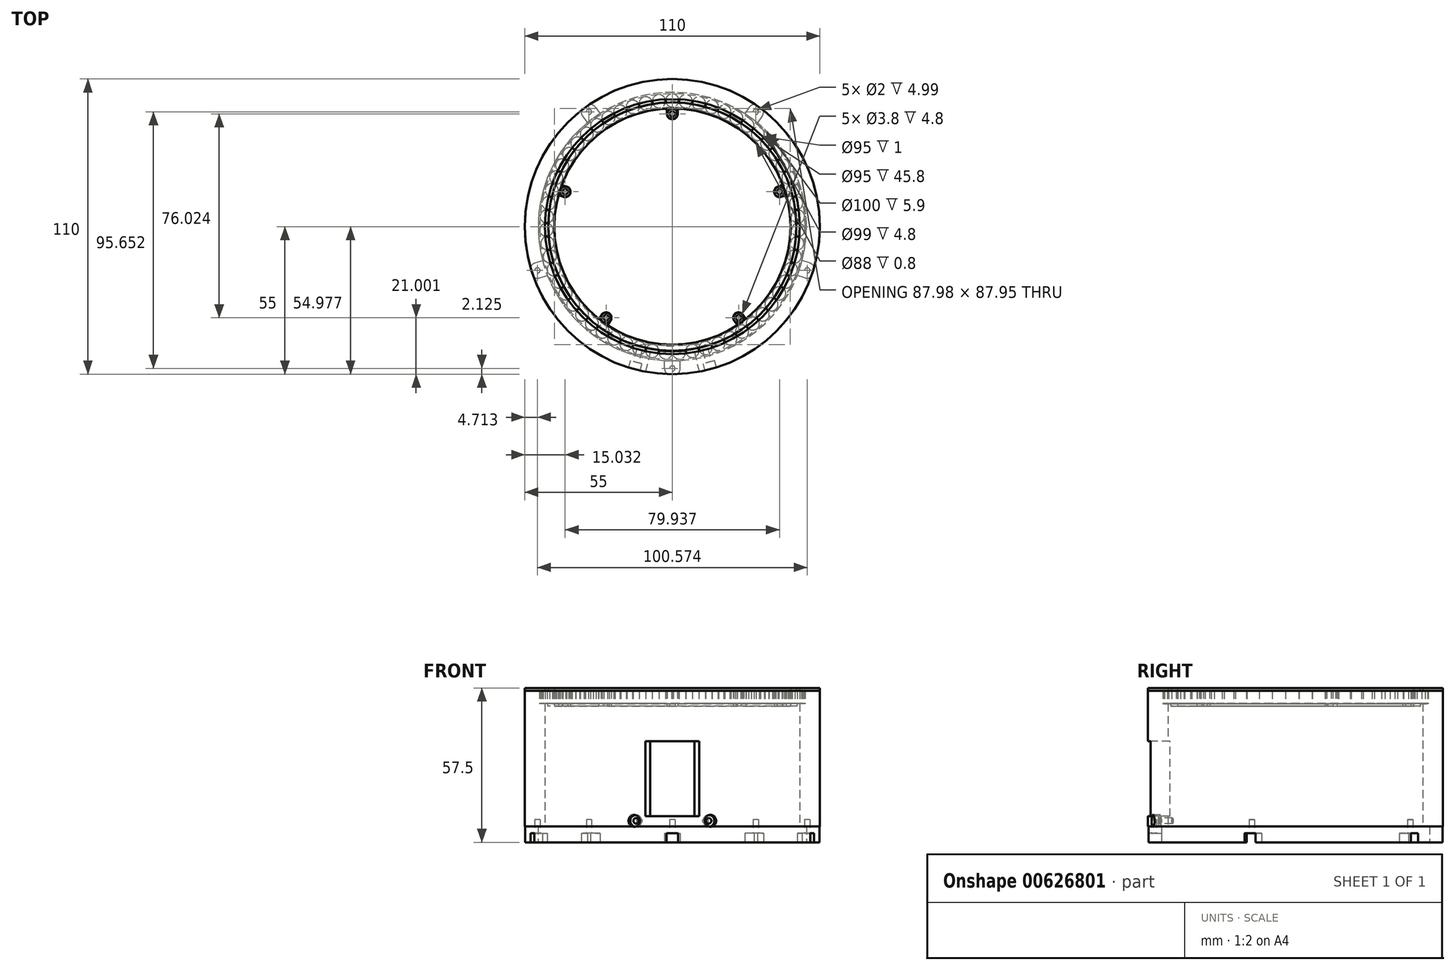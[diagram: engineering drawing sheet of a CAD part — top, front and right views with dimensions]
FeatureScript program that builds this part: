
annotation { "Feature Type Name" : "Feature", "Feature Type Description" : "" }
export const myFeature = defineFeature(function(context is Context, id is Id, definition is map)
    precondition{}
    {
        {
            var Q0;
            Q0=qCreatedBy(makeId("Top.planeOp"),FACE);
            var sketch = newSketch(context, id + "F0", { "sketchPlane" : qUnion([Q0])});
            skCircle(sketch, "E0", {"center": v(0, 0) * mm, "radius": 54.84 * mm});
            skCircle(sketch, "E1", {"center": v(0, 0) * mm, "radius": 50 * mm});
            skLineSegment(sketch, "E2", {"start": v(0, 0) * mm, "end": v(0, -52.87) * mm, "construction": true});
            skCircle(sketch, "E3", {"center": v(0, -52.88) * mm, "radius": 1 * mm});
            skCircle(sketch, "E4.1.0", {"center": v(50.29, -16.34) * mm, "radius": 1 * mm});
            skCircle(sketch, "E4.2.0", {"center": v(31.08, 42.78) * mm, "radius": 1 * mm});
            skCircle(sketch, "E4.3.0", {"center": v(-31.08, 42.78) * mm, "radius": 1 * mm});
            skCircle(sketch, "E4.4.0", {"center": v(-50.29, -16.34) * mm, "radius": 1 * mm});
            skCircle(sketch, "E5", {"center": v(0, -52.88) * mm, "radius": 2.9 * mm});
            skLineSegment(sketch, "E6", {"start": v(2.9, -52.88) * mm, "end": v(2.9, -49.89) * mm});
            skLineSegment(sketch, "E7.1.0", {"start": v(49.4, -19.1) * mm, "end": v(46.6, -18.19) * mm});
            skLineSegment(sketch, "E7.1.1", {"start": v(51.18, -13.58) * mm, "end": v(48.34, -12.66) * mm});
            skCircle(sketch, "E7.1.2", {"center": v(50.29, -16.34) * mm, "radius": 2.9 * mm});
            skLineSegment(sketch, "E7.2.0", {"start": v(33.43, 41.07) * mm, "end": v(31.7, 38.7) * mm});
            skLineSegment(sketch, "E7.2.1", {"start": v(28.73, 44.48) * mm, "end": v(26.98, 42.06) * mm});
            skCircle(sketch, "E7.2.2", {"center": v(31.08, 42.78) * mm, "radius": 2.9 * mm});
            skLineSegment(sketch, "E7.3.0", {"start": v(-28.73, 44.48) * mm, "end": v(-27, 42.1) * mm});
            skLineSegment(sketch, "E7.3.1", {"start": v(-33.43, 41.07) * mm, "end": v(-31.67, 38.65) * mm});
            skCircle(sketch, "E7.3.2", {"center": v(-31.08, 42.78) * mm, "radius": 2.9 * mm});
            skLineSegment(sketch, "E7.4.0", {"start": v(-51.18, -13.58) * mm, "end": v(-48.39, -12.67) * mm});
            skLineSegment(sketch, "E7.4.1", {"start": v(-49.4, -19.1) * mm, "end": v(-46.55, -18.17) * mm});
            skCircle(sketch, "E7.4.2", {"center": v(-50.29, -16.34) * mm, "radius": 2.9 * mm});
            skLineSegment(sketch, "E8", {"start": v(-2.9, -52.88) * mm, "end": v(-2.9, -49.92) * mm});
            skLineSegment(sketch, "E9.1.0", {"start": v(49.4, -19.1) * mm, "end": v(46.58, -18.18) * mm});
            skLineSegment(sketch, "E9.2.0", {"start": v(33.43, 41.07) * mm, "end": v(31.69, 38.68) * mm});
            skLineSegment(sketch, "E9.3.0", {"start": v(-28.73, 44.48) * mm, "end": v(-27, 42.09) * mm});
            skLineSegment(sketch, "E9.4.0", {"start": v(-51.18, -13.58) * mm, "end": v(-48.37, -12.67) * mm});
            skSolve(sketch);
        }
        {
            var Q0;
            {var subQ0=sQuery(id+"F0.wireOp",EDGE,"E8");Q0=makeQuery(id+"F0.imprint","IMPRINT",FACE,{"disambiguationData":[TD([[makeQuery(id+"F0.imprint","IMPRINT",EDGE,{"derivedFrom":subQ0}),1.0]])]});}
            var Q1;
            {var subQ9=sQuery(id+"F0.wireOp",EDGE,"E9.1.0");var subQ12=makeQuery(id+"F0.imprint","IMPRINT",VERTEX,{"derivedFrom":subQ9});Q1=makeQuery(id+"F0.imprint","IMPRINT",FACE,{"disambiguationData":[TD([[makeQuery(id+"F0.imprint","IMPRINT",EDGE,{"disambiguationData":[TD([[subQ12,1.0]])],"derivedFrom":subQ9}),1.0]])]});}
            var Q2;
            {var subQ7=sQuery(id+"F0.wireOp",EDGE,"E9.4.0");var subQ12=makeQuery(id+"F0.imprint","IMPRINT",VERTEX,{"derivedFrom":subQ7});Q2=makeQuery(id+"F0.imprint","IMPRINT",FACE,{"disambiguationData":[TD([[makeQuery(id+"F0.imprint","IMPRINT",EDGE,{"disambiguationData":[TD([[subQ12,1.0]])],"derivedFrom":subQ7}),1.0]])]});}
            var Q3;
            {var subQ5=sQuery(id+"F0.wireOp",EDGE,"E9.2.0");var subQ11=makeQuery(id+"F0.imprint","IMPRINT",VERTEX,{"derivedFrom":subQ5});Q3=makeQuery(id+"F0.imprint","IMPRINT",FACE,{"disambiguationData":[TD([[makeQuery(id+"F0.imprint","IMPRINT",EDGE,{"disambiguationData":[TD([[subQ11,1.0]])],"derivedFrom":subQ5}),1.0]])]});}
            var Q4;
            {var subQ7=sQuery(id+"F0.wireOp",EDGE,"E9.3.0");var subQ12=makeQuery(id+"F0.imprint","IMPRINT",VERTEX,{"derivedFrom":subQ7});Q4=makeQuery(id+"F0.imprint","IMPRINT",FACE,{"disambiguationData":[TD([[makeQuery(id+"F0.imprint","IMPRINT",EDGE,{"disambiguationData":[TD([[subQ12,1.0]])],"derivedFrom":subQ7}),1.0]])]});}
            extrude(context, id + "F1", {"entities" : qUnion([Q0, Q1, Q2, Q3, Q4]), "depth" : 3.5 * mm, "offsetDistance" : 25 * mm, "hasSecondDirection" : true, "secondDirectionOppositeDirection" : false, "secondDirectionDepth" : 0.1 * mm});
        }
        {
            var Q0;
            Q0=makeQuery(id+"F1.opExtrude","CAP_FACE",FACE,{"disambiguationData":[OSD([sQuery(id+"F0.wireOp",EDGE,"E0"),sQuery(id+"F0.wireOp",EDGE,"E1"),sQuery(id+"F0.wireOp",EDGE,"E7.3.1"),sQuery(id+"F0.wireOp",EDGE,"E7.3.2"),sQuery(id+"F0.wireOp",EDGE,"E9.4.0"),sQuery(id+"F0.wireOp",EDGE,"E7.4.2")])],"isStart":false});
            var sketch = newSketch(context, id + "F2", { "sketchPlane" : qUnion([Q0])});
            skCircle(sketch, "E10", {"center": v(0, 0) * mm, "radius": 54.84 * mm});
            skCircle(sketch, "E11", {"center": v(0, 0) * mm, "radius": 50 * mm});
            skLineSegment(sketch, "E12", {"start": v(0, 0) * mm, "end": v(0, -52.88) * mm, "construction": true});
            skCircle(sketch, "E13", {"center": v(0, -52.88) * mm, "radius": 1 * mm});
            skCircle(sketch, "E14.1.0", {"center": v(50.29, -16.34) * mm, "radius": 1 * mm});
            skCircle(sketch, "E14.2.0", {"center": v(31.08, 42.78) * mm, "radius": 1 * mm});
            skCircle(sketch, "E14.3.0", {"center": v(-31.08, 42.78) * mm, "radius": 1 * mm});
            skCircle(sketch, "E14.4.0", {"center": v(-50.29, -16.34) * mm, "radius": 1 * mm});
            skSolve(sketch);
        }
        {
            var Q0;
            Q0=makeQuery(id+"F2.imprint","IMPRINT",FACE,{"disambiguationData":[TD([[makeQuery(id+"F2.imprint","IMPRINT",EDGE,{"derivedFrom":sQuery(id+"F2.wireOp",EDGE,"E13")}),-1.0]])]});
            var Q1;
            {var subQ1=sQuery(id+"F0.wireOp",EDGE,"E7.3.1");var subQ7=makeQuery(id+"F1.opExtrude","CAP_EDGE",EDGE,{"disambiguationData":[OSD([subQ1])],"isStart":false});Q1=makeQuery(id+"F2.imprint","IMPRINT",FACE,{"disambiguationData":[TD([[makeQuery(id+"F2.imprint","IMPRINT",EDGE,{"derivedFrom":subQ7}),-1.0]])]});}
            extrude(context, id + "F3", {"entities" : qUnion([Q0, Q1]), "operationType" : NewBodyOperationType.ADD, "depth" : 2.5 * mm, "offsetDistance" : 25 * mm});
        }
        {
            var Q0;
            Q0=makeQuery(id+"F3.opExtrude","CAP_FACE",FACE,{"disambiguationData":[OSD([sQuery(id+"F2.wireOp",EDGE,"E10"),sQuery(id+"F2.wireOp",EDGE,"E11"),sQuery(id+"F2.wireOp",EDGE,"E13"),sQuery(id+"F2.wireOp",EDGE,"E14.1.0"),sQuery(id+"F2.wireOp",EDGE,"E14.2.0"),sQuery(id+"F2.wireOp",EDGE,"E14.3.0"),sQuery(id+"F2.wireOp",EDGE,"E14.4.0")])],"isStart":false});
            var sketch = newSketch(context, id + "F4", { "sketchPlane" : qUnion([Q0])});
            skCircle(sketch, "E15", {"center": v(0, 0) * mm, "radius": 55 * mm});
            skCircle(sketch, "E16", {"center": v(0, 0) * mm, "radius": 47.5 * mm});
            skLineSegment(sketch, "E17", {"start": v(0, 0) * mm, "end": v(0, -52.88) * mm, "construction": true});
            skCircle(sketch, "E18", {"center": v(0, -52.88) * mm, "radius": 1 * mm});
            skCircle(sketch, "E19.1.0", {"center": v(50.29, -16.34) * mm, "radius": 1 * mm});
            skCircle(sketch, "E19.2.0", {"center": v(31.08, 42.78) * mm, "radius": 1 * mm});
            skCircle(sketch, "E19.3.0", {"center": v(-31.08, 42.78) * mm, "radius": 1 * mm});
            skCircle(sketch, "E19.4.0", {"center": v(-50.29, -16.34) * mm, "radius": 1 * mm});
            skSolve(sketch);
        }
        {
            var Q0;
            Q0 = qSketchRegion(id + "F4", true);
            extrude(context, id + "F5", {"entities" : qUnion([Q0]), "operationType" : NewBodyOperationType.ADD, "depth" : 2.5 * mm, "offsetDistance" : 25 * mm});
        }
        {
            var Q0;
            Q0=makeQuery(id+"F5.opExtrude","CAP_FACE",FACE,{"disambiguationData":[OSD([sQuery(id+"F4.wireOp",EDGE,"E15"),sQuery(id+"F4.wireOp",EDGE,"E16"),sQuery(id+"F4.wireOp",EDGE,"E18"),sQuery(id+"F4.wireOp",EDGE,"E19.1.0"),sQuery(id+"F4.wireOp",EDGE,"E19.2.0"),sQuery(id+"F4.wireOp",EDGE,"E19.3.0"),sQuery(id+"F4.wireOp",EDGE,"E19.4.0")])],"isStart":false});
            var sketch = newSketch(context, id + "F6", { "sketchPlane" : qUnion([Q0])});
            skCircle(sketch, "E20", {"center": v(0, 0) * mm, "radius": 55 * mm});
            skCircle(sketch, "E21", {"center": v(0, 0) * mm, "radius": 47.5 * mm});
            skSolve(sketch);
        }
        {
            var Q0;
            Q0 = qSketchRegion(id + "F6", true);
            extrude(context, id + "F7", {"entities" : qUnion([Q0]), "operationType" : NewBodyOperationType.ADD, "depth" : 42.3 * mm, "offsetDistance" : 25 * mm});
        }
        {
            var Q0;
            Q0=makeQuery(id+"F7.opExtrude","CAP_FACE",FACE,{"disambiguationData":[OSD([sQuery(id+"F6.wireOp",EDGE,"E20"),sQuery(id+"F6.wireOp",EDGE,"E21")])],"isStart":false});
            var sketch = newSketch(context, id + "F8", { "sketchPlane" : qUnion([Q0])});
            skLineSegment(sketch, "E22", {"start": v(0, 0) * mm, "end": v(0, -55) * mm, "construction": true});
            skCircle(sketch, "E23", {"center": v(0, 0) * mm, "radius": 55 * mm});
            skCircle(sketch, "E24", {"center": v(0, 0) * mm, "radius": 47.5 * mm});
            skLineSegment(sketch, "E25", {"start": v(0, 0) * mm, "end": v(8.25, -46.78) * mm, "construction": true});
            skLineSegment(sketch, "E26", {"start": v(0, 0) * mm, "end": v(-8.25, -46.78) * mm, "construction": true});
            skLineSegment(sketch, "E27", {"start": v(-8.25, -46.78) * mm, "end": v(-10, -54.08) * mm});
            skLineSegment(sketch, "E28", {"start": v(8.25, -46.78) * mm, "end": v(10, -54.08) * mm});
            skSolve(sketch);
        }
        {
            var Q0;
            {var subQ0=sQuery(id+"F8.wireOp",EDGE,"E27");Q0=makeQuery(id+"F8.imprint","IMPRINT",FACE,{"disambiguationData":[TD([[makeQuery(id+"F8.imprint","IMPRINT",EDGE,{"derivedFrom":subQ0}),1.0]])]});}
            extrude(context, id + "F9", {"entities" : qUnion([Q0]), "operationType" : NewBodyOperationType.REMOVE, "oppositeDirection" : true, "depth" : 41 * mm, "offsetDistance" : 25 * mm, "hasSecondDirection" : true, "secondDirectionOppositeDirection" : true, "secondDirectionDepth" : 13 * mm});
        }
        {
            var Q0;
            Q0=qCreatedBy(makeId("Front.planeOp"),FACE);
            var sketch = newSketch(context, id + "F10", { "sketchPlane" : qUnion([Q0])});
            skLineSegment(sketch, "E29", {"start": v(0, 0) * mm, "end": v(0, 3.5) * mm, "construction": true});
            skLineSegment(sketch, "E30", {"start": v(0, 3.5) * mm, "end": v(0, 8.1) * mm, "construction": true});
            skSolve(sketch);
        }
        {
            var Q0;
            Q0=qCreatedBy(makeId("Top.planeOp"),FACE);
            cPlane(context, id + "F11", {"entities" : qUnion([Q0]), "cplaneType" : CPlaneType.OFFSET, "offset" : 8.1 * mm, "width" : 150 * mm, "height" : 150 * mm});
        }
        {
            var Q0;
            Q0=qCreatedBy(id+"F11.planeOp",FACE);
            var sketch = newSketch(context, id + "F12", { "sketchPlane" : qUnion([Q0])});
            skLineSegment(sketch, "E31", {"start": v(0, 0) * mm, "end": v(0, -55.35) * mm, "construction": true});
            skCircle(sketch, "E32", {"center": v(0, 0) * mm, "radius": 55.35 * mm, "construction": true});
            skLineSegment(sketch, "E33", {"start": v(0, 0) * mm, "end": v(-14.33, -53.46) * mm, "construction": true});
            skLineSegment(sketch, "E34", {"start": v(0, 0) * mm, "end": v(14.33, -53.46) * mm, "construction": true});
            skLineSegment(sketch, "E35", {"start": v(-0.35, -57.2) * mm, "end": v(-14.33, -53.46) * mm, "construction": true});
            skLineSegment(sketch, "E36", {"start": v(14.33, -53.46) * mm, "end": v(0.35, -57.2) * mm, "construction": true});
            skSolve(sketch);
        }
        {
            var Q0;
            Q0=sQuery(id+"F12.wireOp",EDGE,"E35");
            cPlane(context, id + "F13", {"entities" : qUnion([Q0]), "cplaneType" : CPlaneType.LINE_ANGLE, "offset" : 25 * mm, "angle" : 0 * degree, "width" : 150 * mm, "height" : 150 * mm});
        }
        {
            var Q0;
            Q0=sQuery(id+"F12.wireOp",EDGE,"E36");
            cPlane(context, id + "F14", {"entities" : qUnion([Q0]), "cplaneType" : CPlaneType.LINE_ANGLE, "offset" : 25 * mm, "angle" : 0 * degree, "width" : 150 * mm, "height" : 150 * mm});
        }
        {
            var Q0;
            Q0=qCreatedBy(id+"F14.planeOp",FACE);
            var sketch = newSketch(context, id + "F15", { "sketchPlane" : qUnion([Q0])});
            skCircle(sketch, "E37", {"center": v(0, 8.1) * mm, "radius": 2.2 * mm});
            skSolve(sketch);
        }
        {
            var Q0;
            Q0 = qSketchRegion(id + "F15", true);
            extrude(context, id + "F16", {"entities" : qUnion([Q0]), "operationType" : NewBodyOperationType.REMOVE, "oppositeDirection" : true, "depth" : 3 * mm, "offsetDistance" : 25 * mm});
        }
        {
            var Q0;
            Q0=makeQuery(id+"F16.boolean.opBoolean","COPY",FACE,{"derivedFrom":makeQuery(id+"F16.opExtrude","CAP_FACE",FACE,{"disambiguationData":[OSD([sQuery(id+"F15.wireOp",EDGE,"E37")])],"isStart":false})});
            var sketch = newSketch(context, id + "F17", { "sketchPlane" : qUnion([Q0])});
            skPoint(sketch, "E38", {"position": v(0, 8.1) * mm});
            skCircle(sketch, "E39", {"center": v(0, 8.1) * mm, "radius": 1.02 * mm});
            skSolve(sketch);
        }
        {
            var Q0;
            Q0=makeQuery(id+"F17.imprint","IMPRINT",FACE,{"disambiguationData":[TD([[makeQuery(id+"F17.imprint","IMPRINT",EDGE,{"derivedFrom":sQuery(id+"F17.wireOp",EDGE,"E39")}),1.0]])]});
            extrude(context, id + "F18", {"entities" : qUnion([Q0]), "operationType" : NewBodyOperationType.REMOVE, "oppositeDirection" : true, "depth" : 5.5 * mm, "offsetDistance" : 25 * mm});
        }
        {
            var Q0;
            Q0=qCreatedBy(id+"F13.planeOp",FACE);
            var sketch = newSketch(context, id + "F19", { "sketchPlane" : qUnion([Q0])});
            skCircle(sketch, "E40", {"center": v(0, 8.1) * mm, "radius": 2.2 * mm});
            skSolve(sketch);
        }
        {
            var Q0;
            Q0=makeQuery(id+"F19.imprint","IMPRINT",FACE,{"disambiguationData":[TD([[makeQuery(id+"F19.imprint","IMPRINT",EDGE,{"derivedFrom":sQuery(id+"F19.wireOp",EDGE,"E40")}),1.0]])]});
            extrude(context, id + "F20", {"entities" : qUnion([Q0]), "operationType" : NewBodyOperationType.REMOVE, "oppositeDirection" : true, "depth" : 3 * mm, "offsetDistance" : 25 * mm});
        }
        {
            var Q0;
            Q0=makeQuery(id+"F20.boolean.opBoolean","COPY",FACE,{"derivedFrom":makeQuery(id+"F20.opExtrude","CAP_FACE",FACE,{"disambiguationData":[OSD([sQuery(id+"F19.wireOp",EDGE,"E40")])],"isStart":false})});
            var sketch = newSketch(context, id + "F21", { "sketchPlane" : qUnion([Q0])});
            skPoint(sketch, "E41", {"position": v(0, 8.1) * mm});
            skCircle(sketch, "E42", {"center": v(0, 8.1) * mm, "radius": 1.02 * mm});
            skSolve(sketch);
        }
        {
            var Q0;
            Q0 = qSketchRegion(id + "F21", true);
            extrude(context, id + "F22", {"entities" : qUnion([Q0]), "operationType" : NewBodyOperationType.REMOVE, "oppositeDirection" : true, "depth" : 5 * mm, "offsetDistance" : 25 * mm});
        }
        {
            var Q0;
            Q0=makeQuery(id+"F7.opExtrude","CAP_FACE",FACE,{"disambiguationData":[OSD([sQuery(id+"F6.wireOp",EDGE,"E20"),sQuery(id+"F6.wireOp",EDGE,"E21")])],"isStart":false});
            var sketch = newSketch(context, id + "F23", { "sketchPlane" : qUnion([Q0])});
            skCircle(sketch, "E43", {"center": v(0, 0) * mm, "radius": 50 * mm});
            skCircle(sketch, "E44", {"center": v(0, 0) * mm, "radius": 47.5 * mm});
            skLineSegment(sketch, "E45", {"start": v(0, 0) * mm, "end": v(0, 47.5) * mm, "construction": true});
            skLineSegment(sketch, "E46", {"start": v(0, 47.5) * mm, "end": v(0, 46.5) * mm, "construction": true});
            skCircle(sketch, "E47", {"center": v(0, 0) * mm, "radius": 46.5 * mm});
            skPoint(sketch, "E48", {"position": v(0, 44) * mm});
            skCircle(sketch, "E49", {"center": v(0, 0) * mm, "radius": 44 * mm});
            skPoint(sketch, "E50", {"position": v(0, 42) * mm});
            skCircle(sketch, "E51", {"center": v(0, 42) * mm, "radius": 2 * mm});
            skCircle(sketch, "E52", {"center": v(0, 42) * mm, "radius": 1.9 * mm});
            skCircle(sketch, "E53", {"center": v(0, 42) * mm, "radius": 1 * mm});
            skLineSegment(sketch, "E54", {"start": v(-2, 42) * mm, "end": v(-2, 43.95) * mm});
            skLineSegment(sketch, "E55", {"start": v(2, 42) * mm, "end": v(2.01, 43.95) * mm});
            skLineSegment(sketch, "E56.1.0", {"start": v(-40.56, 11.08) * mm, "end": v(-42.42, 11.68) * mm});
            skLineSegment(sketch, "E56.1.1", {"start": v(-39.33, 14.88) * mm, "end": v(-41.18, 15.5) * mm});
            skCircle(sketch, "E56.1.2", {"center": v(-39.94, 12.98) * mm, "radius": 1 * mm});
            skCircle(sketch, "E56.1.3", {"center": v(-39.94, 12.98) * mm, "radius": 1.9 * mm});
            skCircle(sketch, "E56.1.4", {"center": v(-39.94, 12.98) * mm, "radius": 2 * mm});
            skLineSegment(sketch, "E56.2.0", {"start": v(-23.07, -35.15) * mm, "end": v(-24.22, -36.74) * mm});
            skLineSegment(sketch, "E56.2.1", {"start": v(-26.3, -32.8) * mm, "end": v(-27.46, -34.38) * mm});
            skCircle(sketch, "E56.2.2", {"center": v(-24.69, -33.98) * mm, "radius": 1 * mm});
            skCircle(sketch, "E56.2.3", {"center": v(-24.69, -33.98) * mm, "radius": 1.9 * mm});
            skCircle(sketch, "E56.2.4", {"center": v(-24.69, -33.98) * mm, "radius": 2 * mm});
            skLineSegment(sketch, "E56.3.0", {"start": v(26.3, -32.8) * mm, "end": v(27.45, -34.38) * mm});
            skLineSegment(sketch, "E56.3.1", {"start": v(23.07, -35.15) * mm, "end": v(24.2, -36.74) * mm});
            skCircle(sketch, "E56.3.2", {"center": v(24.69, -33.98) * mm, "radius": 1 * mm});
            skCircle(sketch, "E56.3.3", {"center": v(24.69, -33.98) * mm, "radius": 1.9 * mm});
            skCircle(sketch, "E56.3.4", {"center": v(24.69, -33.98) * mm, "radius": 2 * mm});
            skLineSegment(sketch, "E56.4.0", {"start": v(39.33, 14.88) * mm, "end": v(41.19, 15.48) * mm});
            skLineSegment(sketch, "E56.4.1", {"start": v(40.56, 11.08) * mm, "end": v(42.42, 11.67) * mm});
            skCircle(sketch, "E56.4.2", {"center": v(39.94, 12.98) * mm, "radius": 1 * mm});
            skCircle(sketch, "E56.4.3", {"center": v(39.94, 12.98) * mm, "radius": 1.9 * mm});
            skCircle(sketch, "E56.4.4", {"center": v(39.94, 12.98) * mm, "radius": 2 * mm});
            skCircle(sketch, "E57", {"center": v(0, 42) * mm, "radius": 1.56 * mm});
            skSolve(sketch);
        }
        {
            var Q0;
            Q0 = qSketchRegion(id + "F23", true);
            var Q1;
            Q1=makeQuery(id+"F23.imprint","IMPRINT",FACE,{"disambiguationData":[TD([[makeQuery(id+"F23.imprint","IMPRINT",EDGE,{"derivedFrom":sQuery(id+"F23.wireOp",EDGE,"E47")}),1.0]])]});
            var Q2;
            {var subQ0=sQuery(id+"F23.wireOp",EDGE,"E54");Q2=makeQuery(id+"F23.imprint","IMPRINT",FACE,{"disambiguationData":[TD([[makeQuery(id+"F23.imprint","IMPRINT",EDGE,{"derivedFrom":subQ0}),-1.0]])]});}
            var Q3;
            {var subQ0=sQuery(id+"F23.wireOp",EDGE,"E55");Q3=makeQuery(id+"F23.imprint","IMPRINT",FACE,{"disambiguationData":[TD([[makeQuery(id+"F23.imprint","IMPRINT",EDGE,{"derivedFrom":subQ0}),1.0]])]});}
            var Q4;
            Q4=makeQuery(id+"F23.imprint","IMPRINT",FACE,{"disambiguationData":[TD([[makeQuery(id+"F23.imprint","IMPRINT",EDGE,{"derivedFrom":sQuery(id+"F23.wireOp",EDGE,"E52")}),-1.0]])]});
            var Q5;
            Q5=makeQuery(id+"F23.imprint","IMPRINT",FACE,{"disambiguationData":[TD([[makeQuery(id+"F23.imprint","IMPRINT",EDGE,{"derivedFrom":sQuery(id+"F23.wireOp",EDGE,"E52")}),1.0]])]});
            var Q6;
            {var subQ0=sQuery(id+"F23.wireOp",EDGE,"E56.4.0");Q6=makeQuery(id+"F23.imprint","IMPRINT",FACE,{"disambiguationData":[TD([[makeQuery(id+"F23.imprint","IMPRINT",EDGE,{"derivedFrom":subQ0}),-1.0]])]});}
            var Q7;
            {var subQ0=sQuery(id+"F23.wireOp",EDGE,"E56.4.1");Q7=makeQuery(id+"F23.imprint","IMPRINT",FACE,{"disambiguationData":[TD([[makeQuery(id+"F23.imprint","IMPRINT",EDGE,{"derivedFrom":subQ0}),1.0]])]});}
            var Q8;
            Q8=makeQuery(id+"F23.imprint","IMPRINT",FACE,{"disambiguationData":[TD([[makeQuery(id+"F23.imprint","IMPRINT",EDGE,{"derivedFrom":sQuery(id+"F23.wireOp",EDGE,"E56.4.3")}),-1.0]])]});
            var Q9;
            Q9=makeQuery(id+"F23.imprint","IMPRINT",FACE,{"disambiguationData":[TD([[makeQuery(id+"F23.imprint","IMPRINT",EDGE,{"derivedFrom":sQuery(id+"F23.wireOp",EDGE,"E56.4.2")}),-1.0]])]});
            var Q10;
            {var subQ0=sQuery(id+"F23.wireOp",EDGE,"E56.3.0");Q10=makeQuery(id+"F23.imprint","IMPRINT",FACE,{"disambiguationData":[TD([[makeQuery(id+"F23.imprint","IMPRINT",EDGE,{"derivedFrom":subQ0}),-1.0]])]});}
            var Q11;
            {var subQ0=sQuery(id+"F23.wireOp",EDGE,"E56.3.1");Q11=makeQuery(id+"F23.imprint","IMPRINT",FACE,{"disambiguationData":[TD([[makeQuery(id+"F23.imprint","IMPRINT",EDGE,{"derivedFrom":subQ0}),1.0]])]});}
            var Q12;
            Q12=makeQuery(id+"F23.imprint","IMPRINT",FACE,{"disambiguationData":[TD([[makeQuery(id+"F23.imprint","IMPRINT",EDGE,{"derivedFrom":sQuery(id+"F23.wireOp",EDGE,"E56.3.3")}),-1.0]])]});
            var Q13;
            Q13=makeQuery(id+"F23.imprint","IMPRINT",FACE,{"disambiguationData":[TD([[makeQuery(id+"F23.imprint","IMPRINT",EDGE,{"derivedFrom":sQuery(id+"F23.wireOp",EDGE,"E56.3.2")}),-1.0]])]});
            var Q14;
            {var subQ0=sQuery(id+"F23.wireOp",EDGE,"E56.2.1");Q14=makeQuery(id+"F23.imprint","IMPRINT",FACE,{"disambiguationData":[TD([[makeQuery(id+"F23.imprint","IMPRINT",EDGE,{"derivedFrom":subQ0}),1.0]])]});}
            var Q15;
            {var subQ0=sQuery(id+"F23.wireOp",EDGE,"E56.2.0");Q15=makeQuery(id+"F23.imprint","IMPRINT",FACE,{"disambiguationData":[TD([[makeQuery(id+"F23.imprint","IMPRINT",EDGE,{"derivedFrom":subQ0}),-1.0]])]});}
            var Q16;
            Q16=makeQuery(id+"F23.imprint","IMPRINT",FACE,{"disambiguationData":[TD([[makeQuery(id+"F23.imprint","IMPRINT",EDGE,{"derivedFrom":sQuery(id+"F23.wireOp",EDGE,"E56.2.2")}),-1.0]])]});
            var Q17;
            Q17=makeQuery(id+"F23.imprint","IMPRINT",FACE,{"disambiguationData":[TD([[makeQuery(id+"F23.imprint","IMPRINT",EDGE,{"derivedFrom":sQuery(id+"F23.wireOp",EDGE,"E56.2.3")}),-1.0]])]});
            var Q18;
            {var subQ0=sQuery(id+"F23.wireOp",EDGE,"E56.1.1");Q18=makeQuery(id+"F23.imprint","IMPRINT",FACE,{"disambiguationData":[TD([[makeQuery(id+"F23.imprint","IMPRINT",EDGE,{"derivedFrom":subQ0}),1.0]])]});}
            var Q19;
            Q19=makeQuery(id+"F23.imprint","IMPRINT",FACE,{"disambiguationData":[TD([[makeQuery(id+"F23.imprint","IMPRINT",EDGE,{"derivedFrom":sQuery(id+"F23.wireOp",EDGE,"E56.1.3")}),-1.0]])]});
            var Q20;
            Q20=makeQuery(id+"F23.imprint","IMPRINT",FACE,{"disambiguationData":[TD([[makeQuery(id+"F23.imprint","IMPRINT",EDGE,{"derivedFrom":sQuery(id+"F23.wireOp",EDGE,"E56.1.2")}),-1.0]])]});
            var Q21;
            {var subQ0=sQuery(id+"F23.wireOp",EDGE,"E56.1.0");Q21=makeQuery(id+"F23.imprint","IMPRINT",FACE,{"disambiguationData":[TD([[makeQuery(id+"F23.imprint","IMPRINT",EDGE,{"derivedFrom":subQ0}),-1.0]])]});}
            var Q22;
            Q22=makeQuery(id+"F23.imprint","IMPRINT",FACE,{"disambiguationData":[TD([[makeQuery(id+"F23.imprint","IMPRINT",EDGE,{"derivedFrom":sQuery(id+"F23.wireOp",EDGE,"E53")}),-1.0]])]});
            extrude(context, id + "F24", {"entities" : qUnion([Q0, Q1, Q2, Q3, Q4, Q5, Q6, Q7, Q8, Q9, Q10, Q11, Q12, Q13, Q14, Q15, Q16, Q17, Q18, Q19, Q20, Q21, Q22]), "operationType" : NewBodyOperationType.ADD, "depth" : 1 * mm, "offsetDistance" : 25 * mm});
        }
        {
            var Q0;
            Q0=makeQuery(id+"F24.opExtrude","CAP_FACE",FACE,{"disambiguationData":[OSD([sQuery(id+"F23.wireOp",EDGE,"E43"),sQuery(id+"F23.wireOp",EDGE,"E44")])],"isStart":false});
            var sketch = newSketch(context, id + "F25", { "sketchPlane" : qUnion([Q0])});
            skCircle(sketch, "E58", {"center": v(0, 0) * mm, "radius": 50 * mm});
            skCircle(sketch, "E59", {"center": v(0, 0) * mm, "radius": 49.5 * mm});
            skCircle(sketch, "E60", {"center": v(0, 0) * mm, "radius": 44 * mm});
            skCircle(sketch, "E61", {"center": v(0, 0) * mm, "radius": 44.5 * mm});
            skLineSegment(sketch, "E62", {"start": v(0, 44.5) * mm, "end": v(0, 49.5) * mm, "construction": true});
            skLineSegment(sketch, "E63", {"start": v(0, 49.5) * mm, "end": v(0, 47) * mm, "construction": true});
            skCircle(sketch, "E64", {"center": v(0, 47) * mm, "radius": 2.45 * mm});
            skCircle(sketch, "E65.1.0", {"center": v(-5, 46.73) * mm, "radius": 2.45 * mm});
            skCircle(sketch, "E65.2.0", {"center": v(-9.93, 45.94) * mm, "radius": 2.45 * mm});
            skCircle(sketch, "E65.3.0", {"center": v(-14.75, 44.62) * mm, "radius": 2.45 * mm});
            skCircle(sketch, "E65.4.0", {"center": v(-19.41, 42.8) * mm, "radius": 2.45 * mm});
            skCircle(sketch, "E65.5.0", {"center": v(-23.85, 40.5) * mm, "radius": 2.45 * mm});
            skCircle(sketch, "E65.6.0", {"center": v(-28.01, 37.73) * mm, "radius": 2.45 * mm});
            skCircle(sketch, "E65.7.0", {"center": v(-31.86, 34.54) * mm, "radius": 2.45 * mm});
            skCircle(sketch, "E65.8.0", {"center": v(-35.35, 30.96) * mm, "radius": 2.45 * mm});
            skCircle(sketch, "E65.9.0", {"center": v(-38.44, 27.03) * mm, "radius": 2.45 * mm});
            skCircle(sketch, "E65.10.0", {"center": v(-41.1, 22.79) * mm, "radius": 2.45 * mm});
            skCircle(sketch, "E65.11.0", {"center": v(-43.28, 18.3) * mm, "radius": 2.45 * mm});
            skCircle(sketch, "E65.12.0", {"center": v(-44.97, 13.59) * mm, "radius": 2.45 * mm});
            skCircle(sketch, "E65.13.0", {"center": v(-46.16, 8.73) * mm, "radius": 2.45 * mm});
            skCircle(sketch, "E65.14.0", {"center": v(-46.83, 3.77) * mm, "radius": 2.45 * mm});
            skCircle(sketch, "E65.15.0", {"center": v(-46.96, -1.23) * mm, "radius": 2.45 * mm});
            skCircle(sketch, "E65.16.0", {"center": v(-46.56, -6.2) * mm, "radius": 2.45 * mm});
            skCircle(sketch, "E65.17.0", {"center": v(-45.63, -11.12) * mm, "radius": 2.45 * mm});
            skCircle(sketch, "E65.18.0", {"center": v(-44.19, -15.91) * mm, "radius": 2.45 * mm});
            skCircle(sketch, "E65.19.0", {"center": v(-42.25, -20.52) * mm, "radius": 2.45 * mm});
            skCircle(sketch, "E65.20.0", {"center": v(-39.82, -24.9) * mm, "radius": 2.45 * mm});
            skCircle(sketch, "E65.21.0", {"center": v(-36.95, -28.98) * mm, "radius": 2.45 * mm});
            skCircle(sketch, "E65.22.0", {"center": v(-33.66, -32.75) * mm, "radius": 2.45 * mm});
            skCircle(sketch, "E65.23.0", {"center": v(-29.98, -36.14) * mm, "radius": 2.45 * mm});
            skCircle(sketch, "E65.24.0", {"center": v(-25.97, -39.12) * mm, "radius": 2.45 * mm});
            skCircle(sketch, "E65.25.0", {"center": v(-21.66, -41.66) * mm, "radius": 2.45 * mm});
            skCircle(sketch, "E65.26.0", {"center": v(-17.1, -43.72) * mm, "radius": 2.45 * mm});
            skCircle(sketch, "E65.27.0", {"center": v(-12.36, -45.3) * mm, "radius": 2.45 * mm});
            skCircle(sketch, "E65.28.0", {"center": v(-7.47, -46.35) * mm, "radius": 2.45 * mm});
            skCircle(sketch, "E65.29.0", {"center": v(-2.5, -46.88) * mm, "radius": 2.45 * mm});
            skCircle(sketch, "E65.30.0", {"center": v(2.5, -46.88) * mm, "radius": 2.45 * mm});
            skCircle(sketch, "E65.31.0", {"center": v(7.47, -46.35) * mm, "radius": 2.45 * mm});
            skCircle(sketch, "E65.32.0", {"center": v(12.36, -45.3) * mm, "radius": 2.45 * mm});
            skCircle(sketch, "E65.33.0", {"center": v(17.1, -43.72) * mm, "radius": 2.45 * mm});
            skCircle(sketch, "E65.34.0", {"center": v(21.66, -41.66) * mm, "radius": 2.45 * mm});
            skCircle(sketch, "E65.35.0", {"center": v(25.97, -39.12) * mm, "radius": 2.45 * mm});
            skCircle(sketch, "E65.36.0", {"center": v(29.98, -36.14) * mm, "radius": 2.45 * mm});
            skCircle(sketch, "E65.37.0", {"center": v(33.66, -32.75) * mm, "radius": 2.45 * mm});
            skCircle(sketch, "E65.38.0", {"center": v(36.95, -28.98) * mm, "radius": 2.45 * mm});
            skCircle(sketch, "E65.39.0", {"center": v(39.82, -24.9) * mm, "radius": 2.45 * mm});
            skCircle(sketch, "E65.40.0", {"center": v(42.25, -20.52) * mm, "radius": 2.45 * mm});
            skCircle(sketch, "E65.41.0", {"center": v(44.19, -15.91) * mm, "radius": 2.45 * mm});
            skCircle(sketch, "E65.42.0", {"center": v(45.63, -11.12) * mm, "radius": 2.45 * mm});
            skCircle(sketch, "E65.43.0", {"center": v(46.56, -6.2) * mm, "radius": 2.45 * mm});
            skCircle(sketch, "E65.44.0", {"center": v(46.96, -1.23) * mm, "radius": 2.45 * mm});
            skCircle(sketch, "E65.45.0", {"center": v(46.83, 3.77) * mm, "radius": 2.45 * mm});
            skCircle(sketch, "E65.46.0", {"center": v(46.16, 8.73) * mm, "radius": 2.45 * mm});
            skCircle(sketch, "E65.47.0", {"center": v(44.97, 13.59) * mm, "radius": 2.45 * mm});
            skCircle(sketch, "E65.48.0", {"center": v(43.28, 18.3) * mm, "radius": 2.45 * mm});
            skCircle(sketch, "E65.49.0", {"center": v(41.1, 22.79) * mm, "radius": 2.45 * mm});
            skCircle(sketch, "E65.50.0", {"center": v(38.44, 27.03) * mm, "radius": 2.45 * mm});
            skCircle(sketch, "E65.51.0", {"center": v(35.35, 30.96) * mm, "radius": 2.45 * mm});
            skCircle(sketch, "E65.52.0", {"center": v(31.86, 34.54) * mm, "radius": 2.45 * mm});
            skCircle(sketch, "E65.53.0", {"center": v(28.01, 37.73) * mm, "radius": 2.45 * mm});
            skCircle(sketch, "E65.54.0", {"center": v(23.85, 40.5) * mm, "radius": 2.45 * mm});
            skCircle(sketch, "E65.55.0", {"center": v(19.41, 42.8) * mm, "radius": 2.45 * mm});
            skCircle(sketch, "E65.56.0", {"center": v(14.75, 44.62) * mm, "radius": 2.45 * mm});
            skCircle(sketch, "E65.57.0", {"center": v(9.93, 45.94) * mm, "radius": 2.45 * mm});
            skCircle(sketch, "E65.58.0", {"center": v(5, 46.73) * mm, "radius": 2.45 * mm});
            skPoint(sketch, "E65.center", {"position": v(0, 0.03) * mm});
            skPoint(sketch, "E66", {"position": v(0, 42.03) * mm});
            skCircle(sketch, "E67", {"center": v(0, 42.03) * mm, "radius": 2 * mm});
            skCircle(sketch, "E68", {"center": v(0, 42.03) * mm, "radius": 1.9 * mm});
            skLineSegment(sketch, "E69", {"start": v(2, 42.03) * mm, "end": v(2, 43.95) * mm});
            skLineSegment(sketch, "E70", {"start": v(-2, 42) * mm, "end": v(-2.03, 43.95) * mm});
            skCircle(sketch, "E71.1.0", {"center": v(-39.97, 12.99) * mm, "radius": 1.9 * mm});
            skCircle(sketch, "E71.1.1", {"center": v(-39.97, 12.99) * mm, "radius": 2 * mm});
            skLineSegment(sketch, "E71.1.2", {"start": v(-39.35, 14.89) * mm, "end": v(-41.19, 15.48) * mm});
            skLineSegment(sketch, "E71.1.3", {"start": v(-40.56, 11.08) * mm, "end": v(-42.43, 11.65) * mm});
            skCircle(sketch, "E71.2.0", {"center": v(-24.7, -34) * mm, "radius": 1.9 * mm});
            skCircle(sketch, "E71.2.1", {"center": v(-24.7, -34) * mm, "radius": 2 * mm});
            skLineSegment(sketch, "E71.2.2", {"start": v(-26.32, -32.82) * mm, "end": v(-27.45, -34.38) * mm});
            skLineSegment(sketch, "E71.2.3", {"start": v(-23.07, -35.15) * mm, "end": v(-24.2, -36.75) * mm});
            skCircle(sketch, "E71.3.0", {"center": v(24.7, -34) * mm, "radius": 1.9 * mm});
            skCircle(sketch, "E71.3.1", {"center": v(24.7, -34) * mm, "radius": 2 * mm});
            skLineSegment(sketch, "E71.3.2", {"start": v(23.08, -35.17) * mm, "end": v(24.22, -36.74) * mm});
            skLineSegment(sketch, "E71.3.3", {"start": v(26.3, -32.8) * mm, "end": v(27.48, -34.37) * mm});
            skCircle(sketch, "E71.4.0", {"center": v(39.97, 12.99) * mm, "radius": 1.9 * mm});
            skCircle(sketch, "E71.4.1", {"center": v(39.97, 12.99) * mm, "radius": 2 * mm});
            skLineSegment(sketch, "E71.4.2", {"start": v(40.59, 11.08) * mm, "end": v(42.42, 11.68) * mm});
            skLineSegment(sketch, "E71.4.3", {"start": v(39.32, 14.88) * mm, "end": v(41.18, 15.51) * mm});
            skSolve(sketch);
        }
        {
            var Q0;
            Q0=makeQuery(id+"F25.imprint","IMPRINT",FACE,{"disambiguationData":[TD([[makeQuery(id+"F25.imprint","IMPRINT",EDGE,{"derivedFrom":sQuery(id+"F25.wireOp",EDGE,"E58")}),1.0]])]});
            var Q1;
            Q1=makeQuery(id+"F25.imprint","IMPRINT",FACE,{"disambiguationData":[TD([[makeQuery(id+"F25.imprint","IMPRINT",EDGE,{"derivedFrom":sQuery(id+"F25.wireOp",EDGE,"E60")}),-1.0]])]});
            var Q2;
            {var subQ0=sQuery(id+"F25.wireOp",EDGE,"E70");Q2=makeQuery(id+"F25.imprint","IMPRINT",FACE,{"disambiguationData":[TD([[makeQuery(id+"F25.imprint","IMPRINT",EDGE,{"derivedFrom":subQ0}),-1.0]])]});}
            var Q3;
            {var subQ0=sQuery(id+"F25.wireOp",EDGE,"E69");Q3=makeQuery(id+"F25.imprint","IMPRINT",FACE,{"disambiguationData":[TD([[makeQuery(id+"F25.imprint","IMPRINT",EDGE,{"derivedFrom":subQ0}),1.0]])]});}
            var Q4;
            Q4=makeQuery(id+"F25.imprint","IMPRINT",FACE,{"disambiguationData":[TD([[makeQuery(id+"F25.imprint","IMPRINT",EDGE,{"derivedFrom":sQuery(id+"F25.wireOp",EDGE,"E68")}),-1.0]])]});
            var Q5;
            {var subQ0=sQuery(id+"F25.wireOp",EDGE,"E71.4.3");Q5=makeQuery(id+"F25.imprint","IMPRINT",FACE,{"disambiguationData":[TD([[makeQuery(id+"F25.imprint","IMPRINT",EDGE,{"derivedFrom":subQ0}),-1.0]])]});}
            var Q6;
            {var subQ0=sQuery(id+"F25.wireOp",EDGE,"E71.4.2");Q6=makeQuery(id+"F25.imprint","IMPRINT",FACE,{"disambiguationData":[TD([[makeQuery(id+"F25.imprint","IMPRINT",EDGE,{"derivedFrom":subQ0}),1.0]])]});}
            var Q7;
            Q7=makeQuery(id+"F25.imprint","IMPRINT",FACE,{"disambiguationData":[TD([[makeQuery(id+"F25.imprint","IMPRINT",EDGE,{"derivedFrom":sQuery(id+"F25.wireOp",EDGE,"E71.4.0")}),-1.0]])]});
            var Q8;
            Q8=makeQuery(id+"F25.imprint","IMPRINT",FACE,{"disambiguationData":[TD([[makeQuery(id+"F25.imprint","IMPRINT",EDGE,{"derivedFrom":sQuery(id+"F25.wireOp",EDGE,"E71.3.0")}),-1.0]])]});
            var Q9;
            {var subQ0=sQuery(id+"F25.wireOp",EDGE,"E71.3.3");Q9=makeQuery(id+"F25.imprint","IMPRINT",FACE,{"disambiguationData":[TD([[makeQuery(id+"F25.imprint","IMPRINT",EDGE,{"derivedFrom":subQ0}),-1.0]])]});}
            var Q10;
            {var subQ0=sQuery(id+"F25.wireOp",EDGE,"E71.3.2");Q10=makeQuery(id+"F25.imprint","IMPRINT",FACE,{"disambiguationData":[TD([[makeQuery(id+"F25.imprint","IMPRINT",EDGE,{"derivedFrom":subQ0}),1.0]])]});}
            var Q11;
            {var subQ0=sQuery(id+"F25.wireOp",EDGE,"E71.2.2");Q11=makeQuery(id+"F25.imprint","IMPRINT",FACE,{"disambiguationData":[TD([[makeQuery(id+"F25.imprint","IMPRINT",EDGE,{"derivedFrom":subQ0}),1.0]])]});}
            var Q12;
            Q12=makeQuery(id+"F25.imprint","IMPRINT",FACE,{"disambiguationData":[TD([[makeQuery(id+"F25.imprint","IMPRINT",EDGE,{"derivedFrom":sQuery(id+"F25.wireOp",EDGE,"E71.2.0")}),-1.0]])]});
            var Q13;
            {var subQ0=sQuery(id+"F25.wireOp",EDGE,"E71.2.3");Q13=makeQuery(id+"F25.imprint","IMPRINT",FACE,{"disambiguationData":[TD([[makeQuery(id+"F25.imprint","IMPRINT",EDGE,{"derivedFrom":subQ0}),-1.0]])]});}
            var Q14;
            {var subQ0=sQuery(id+"F25.wireOp",EDGE,"E71.1.2");Q14=makeQuery(id+"F25.imprint","IMPRINT",FACE,{"disambiguationData":[TD([[makeQuery(id+"F25.imprint","IMPRINT",EDGE,{"derivedFrom":subQ0}),1.0]])]});}
            var Q15;
            {var subQ0=sQuery(id+"F25.wireOp",EDGE,"E71.1.3");Q15=makeQuery(id+"F25.imprint","IMPRINT",FACE,{"disambiguationData":[TD([[makeQuery(id+"F25.imprint","IMPRINT",EDGE,{"derivedFrom":subQ0}),-1.0]])]});}
            var Q16;
            Q16=makeQuery(id+"F25.imprint","IMPRINT",FACE,{"disambiguationData":[TD([[makeQuery(id+"F25.imprint","IMPRINT",EDGE,{"derivedFrom":sQuery(id+"F25.wireOp",EDGE,"E71.1.0")}),-1.0]])]});
            extrude(context, id + "F26", {"entities" : qUnion([Q0, Q1, Q2, Q3, Q4, Q5, Q6, Q7, Q8, Q9, Q10, Q11, Q12, Q13, Q14, Q15, Q16]), "operationType" : NewBodyOperationType.ADD, "depth" : 4.8 * mm, "offsetDistance" : 25 * mm});
        }
        {
            var Q0;
            Q0=makeQuery(id+"F23.imprint","IMPRINT",FACE,{"disambiguationData":[TD([[makeQuery(id+"F23.imprint","IMPRINT",EDGE,{"derivedFrom":sQuery(id+"F23.wireOp",EDGE,"E43")}),-1.0]])]});
            extrude(context, id + "F27", {"entities" : qUnion([Q0]), "operationType" : NewBodyOperationType.ADD, "depth" : 5.8 * mm, "offsetDistance" : 25 * mm});
        }
        {
            var Q0;
            {var subQ0=sQuery(id+"F25.wireOp",EDGE,"E64");var subQ1=makeQuery(id+"F24.opExtrude","CAP_EDGE",EDGE,{"disambiguationData":[OSD([sQuery(id+"F23.wireOp",EDGE,"E44")])],"isStart":false});var subQ2=makeQuery(id+"F25.imprint","INTERSECT",VERTEX,{"disambiguationData":[OD(0.0)],"derivedFrom":[subQ1,subQ0]});Q0=makeQuery(id+"F25.imprint","IMPRINT",FACE,{"disambiguationData":[TD([[makeQuery(id+"F25.imprint","IMPRINT",EDGE,{"disambiguationData":[TD([[subQ2,1.0]])],"derivedFrom":subQ0}),1.0]])]});}
            var Q1;
            {var subQ0=sQuery(id+"F25.wireOp",EDGE,"E65.1.0");var subQ1=makeQuery(id+"F24.opExtrude","CAP_EDGE",EDGE,{"disambiguationData":[OSD([sQuery(id+"F23.wireOp",EDGE,"E44")])],"isStart":false});var subQ2=makeQuery(id+"F25.imprint","INTERSECT",VERTEX,{"disambiguationData":[OD(0.0)],"derivedFrom":[subQ1,subQ0]});Q1=makeQuery(id+"F25.imprint","IMPRINT",FACE,{"disambiguationData":[TD([[makeQuery(id+"F25.imprint","IMPRINT",EDGE,{"disambiguationData":[TD([[subQ2,1.0]])],"derivedFrom":subQ0}),1.0]])]});}
            var Q2;
            {var subQ0=sQuery(id+"F25.wireOp",EDGE,"E65.1.0");var subQ1=makeQuery(id+"F24.opExtrude","CAP_EDGE",EDGE,{"disambiguationData":[OSD([sQuery(id+"F23.wireOp",EDGE,"E44")])],"isStart":false});var subQ2=makeQuery(id+"F25.imprint","INTERSECT",VERTEX,{"disambiguationData":[OD(0.0)],"derivedFrom":[subQ1,subQ0]});Q2=makeQuery(id+"F25.imprint","IMPRINT",FACE,{"disambiguationData":[TD([[makeQuery(id+"F25.imprint","IMPRINT",EDGE,{"disambiguationData":[TD([[subQ2,-1.0]])],"derivedFrom":subQ0}),1.0]])]});}
            var Q3;
            {var subQ0=sQuery(id+"F25.wireOp",EDGE,"E65.2.0");var subQ1=makeQuery(id+"F24.opExtrude","CAP_EDGE",EDGE,{"disambiguationData":[OSD([sQuery(id+"F23.wireOp",EDGE,"E44")])],"isStart":false});var subQ2=makeQuery(id+"F25.imprint","INTERSECT",VERTEX,{"disambiguationData":[OD(0.0)],"derivedFrom":[subQ1,subQ0]});Q3=makeQuery(id+"F25.imprint","IMPRINT",FACE,{"disambiguationData":[TD([[makeQuery(id+"F25.imprint","IMPRINT",EDGE,{"disambiguationData":[TD([[subQ2,-1.0]])],"derivedFrom":subQ0}),1.0]])]});}
            var Q4;
            {var subQ0=sQuery(id+"F25.wireOp",EDGE,"E65.2.0");var subQ1=makeQuery(id+"F24.opExtrude","CAP_EDGE",EDGE,{"disambiguationData":[OSD([sQuery(id+"F23.wireOp",EDGE,"E44")])],"isStart":false});var subQ2=makeQuery(id+"F25.imprint","INTERSECT",VERTEX,{"disambiguationData":[OD(0.0)],"derivedFrom":[subQ1,subQ0]});Q4=makeQuery(id+"F25.imprint","IMPRINT",FACE,{"disambiguationData":[TD([[makeQuery(id+"F25.imprint","IMPRINT",EDGE,{"disambiguationData":[TD([[subQ2,1.0]])],"derivedFrom":subQ0}),1.0]])]});}
            var Q5;
            {var subQ0=sQuery(id+"F25.wireOp",EDGE,"E65.3.0");var subQ1=makeQuery(id+"F24.opExtrude","CAP_EDGE",EDGE,{"disambiguationData":[OSD([sQuery(id+"F23.wireOp",EDGE,"E44")])],"isStart":false});var subQ2=makeQuery(id+"F25.imprint","INTERSECT",VERTEX,{"disambiguationData":[OD(0.0)],"derivedFrom":[subQ1,subQ0]});Q5=makeQuery(id+"F25.imprint","IMPRINT",FACE,{"disambiguationData":[TD([[makeQuery(id+"F25.imprint","IMPRINT",EDGE,{"disambiguationData":[TD([[subQ2,1.0]])],"derivedFrom":subQ0}),1.0]])]});}
            var Q6;
            {var subQ0=sQuery(id+"F25.wireOp",EDGE,"E65.3.0");var subQ1=makeQuery(id+"F24.opExtrude","CAP_EDGE",EDGE,{"disambiguationData":[OSD([sQuery(id+"F23.wireOp",EDGE,"E44")])],"isStart":false});var subQ2=makeQuery(id+"F25.imprint","INTERSECT",VERTEX,{"disambiguationData":[OD(0.0)],"derivedFrom":[subQ1,subQ0]});Q6=makeQuery(id+"F25.imprint","IMPRINT",FACE,{"disambiguationData":[TD([[makeQuery(id+"F25.imprint","IMPRINT",EDGE,{"disambiguationData":[TD([[subQ2,-1.0]])],"derivedFrom":subQ0}),1.0]])]});}
            var Q7;
            {var subQ0=sQuery(id+"F25.wireOp",EDGE,"E64");var subQ1=makeQuery(id+"F24.opExtrude","CAP_EDGE",EDGE,{"disambiguationData":[OSD([sQuery(id+"F23.wireOp",EDGE,"E44")])],"isStart":false});var subQ2=makeQuery(id+"F25.imprint","INTERSECT",VERTEX,{"disambiguationData":[OD(0.0)],"derivedFrom":[subQ1,subQ0]});Q7=makeQuery(id+"F25.imprint","IMPRINT",FACE,{"disambiguationData":[TD([[makeQuery(id+"F25.imprint","IMPRINT",EDGE,{"disambiguationData":[TD([[subQ2,-1.0]])],"derivedFrom":subQ0}),1.0]])]});}
            var Q8;
            {var subQ0=sQuery(id+"F25.wireOp",EDGE,"E65.58.0");var subQ1=makeQuery(id+"F24.opExtrude","CAP_EDGE",EDGE,{"disambiguationData":[OSD([sQuery(id+"F23.wireOp",EDGE,"E44")])],"isStart":false});var subQ2=makeQuery(id+"F25.imprint","INTERSECT",VERTEX,{"disambiguationData":[OD(0.0)],"derivedFrom":[subQ1,subQ0]});Q8=makeQuery(id+"F25.imprint","IMPRINT",FACE,{"disambiguationData":[TD([[makeQuery(id+"F25.imprint","IMPRINT",EDGE,{"disambiguationData":[TD([[subQ2,1.0]])],"derivedFrom":subQ0}),1.0]])]});}
            var Q9;
            {var subQ0=sQuery(id+"F25.wireOp",EDGE,"E65.58.0");var subQ1=makeQuery(id+"F24.opExtrude","CAP_EDGE",EDGE,{"disambiguationData":[OSD([sQuery(id+"F23.wireOp",EDGE,"E44")])],"isStart":false});var subQ2=makeQuery(id+"F25.imprint","INTERSECT",VERTEX,{"disambiguationData":[OD(0.0)],"derivedFrom":[subQ1,subQ0]});Q9=makeQuery(id+"F25.imprint","IMPRINT",FACE,{"disambiguationData":[TD([[makeQuery(id+"F25.imprint","IMPRINT",EDGE,{"disambiguationData":[TD([[subQ2,-1.0]])],"derivedFrom":subQ0}),1.0]])]});}
            var Q10;
            {var subQ0=sQuery(id+"F25.wireOp",EDGE,"E65.57.0");var subQ1=makeQuery(id+"F24.opExtrude","CAP_EDGE",EDGE,{"disambiguationData":[OSD([sQuery(id+"F23.wireOp",EDGE,"E44")])],"isStart":false});var subQ2=makeQuery(id+"F25.imprint","INTERSECT",VERTEX,{"disambiguationData":[OD(0.0)],"derivedFrom":[subQ1,subQ0]});Q10=makeQuery(id+"F25.imprint","IMPRINT",FACE,{"disambiguationData":[TD([[makeQuery(id+"F25.imprint","IMPRINT",EDGE,{"disambiguationData":[TD([[subQ2,-1.0]])],"derivedFrom":subQ0}),1.0]])]});}
            var Q11;
            {var subQ0=sQuery(id+"F25.wireOp",EDGE,"E65.57.0");var subQ1=makeQuery(id+"F24.opExtrude","CAP_EDGE",EDGE,{"disambiguationData":[OSD([sQuery(id+"F23.wireOp",EDGE,"E44")])],"isStart":false});var subQ2=makeQuery(id+"F25.imprint","INTERSECT",VERTEX,{"disambiguationData":[OD(0.0)],"derivedFrom":[subQ1,subQ0]});Q11=makeQuery(id+"F25.imprint","IMPRINT",FACE,{"disambiguationData":[TD([[makeQuery(id+"F25.imprint","IMPRINT",EDGE,{"disambiguationData":[TD([[subQ2,1.0]])],"derivedFrom":subQ0}),1.0]])]});}
            var Q12;
            {var subQ0=sQuery(id+"F25.wireOp",EDGE,"E65.56.0");var subQ1=makeQuery(id+"F24.opExtrude","CAP_EDGE",EDGE,{"disambiguationData":[OSD([sQuery(id+"F23.wireOp",EDGE,"E44")])],"isStart":false});var subQ2=makeQuery(id+"F25.imprint","INTERSECT",VERTEX,{"disambiguationData":[OD(0.0)],"derivedFrom":[subQ1,subQ0]});Q12=makeQuery(id+"F25.imprint","IMPRINT",FACE,{"disambiguationData":[TD([[makeQuery(id+"F25.imprint","IMPRINT",EDGE,{"disambiguationData":[TD([[subQ2,1.0]])],"derivedFrom":subQ0}),1.0]])]});}
            var Q13;
            {var subQ0=sQuery(id+"F25.wireOp",EDGE,"E65.56.0");var subQ1=makeQuery(id+"F24.opExtrude","CAP_EDGE",EDGE,{"disambiguationData":[OSD([sQuery(id+"F23.wireOp",EDGE,"E44")])],"isStart":false});var subQ2=makeQuery(id+"F25.imprint","INTERSECT",VERTEX,{"disambiguationData":[OD(0.0)],"derivedFrom":[subQ1,subQ0]});Q13=makeQuery(id+"F25.imprint","IMPRINT",FACE,{"disambiguationData":[TD([[makeQuery(id+"F25.imprint","IMPRINT",EDGE,{"disambiguationData":[TD([[subQ2,-1.0]])],"derivedFrom":subQ0}),1.0]])]});}
            var Q14;
            {var subQ0=sQuery(id+"F25.wireOp",EDGE,"E65.55.0");var subQ1=makeQuery(id+"F24.opExtrude","CAP_EDGE",EDGE,{"disambiguationData":[OSD([sQuery(id+"F23.wireOp",EDGE,"E44")])],"isStart":false});var subQ2=makeQuery(id+"F25.imprint","INTERSECT",VERTEX,{"disambiguationData":[OD(0.0)],"derivedFrom":[subQ1,subQ0]});Q14=makeQuery(id+"F25.imprint","IMPRINT",FACE,{"disambiguationData":[TD([[makeQuery(id+"F25.imprint","IMPRINT",EDGE,{"disambiguationData":[TD([[subQ2,-1.0]])],"derivedFrom":subQ0}),1.0]])]});}
            var Q15;
            {var subQ0=sQuery(id+"F25.wireOp",EDGE,"E65.55.0");var subQ1=makeQuery(id+"F24.opExtrude","CAP_EDGE",EDGE,{"disambiguationData":[OSD([sQuery(id+"F23.wireOp",EDGE,"E44")])],"isStart":false});var subQ2=makeQuery(id+"F25.imprint","INTERSECT",VERTEX,{"disambiguationData":[OD(0.0)],"derivedFrom":[subQ1,subQ0]});Q15=makeQuery(id+"F25.imprint","IMPRINT",FACE,{"disambiguationData":[TD([[makeQuery(id+"F25.imprint","IMPRINT",EDGE,{"disambiguationData":[TD([[subQ2,1.0]])],"derivedFrom":subQ0}),1.0]])]});}
            var Q16;
            {var subQ0=sQuery(id+"F25.wireOp",EDGE,"E65.54.0");var subQ1=makeQuery(id+"F24.opExtrude","CAP_EDGE",EDGE,{"disambiguationData":[OSD([sQuery(id+"F23.wireOp",EDGE,"E44")])],"isStart":false});var subQ2=makeQuery(id+"F25.imprint","INTERSECT",VERTEX,{"disambiguationData":[OD(0.0)],"derivedFrom":[subQ1,subQ0]});Q16=makeQuery(id+"F25.imprint","IMPRINT",FACE,{"disambiguationData":[TD([[makeQuery(id+"F25.imprint","IMPRINT",EDGE,{"disambiguationData":[TD([[subQ2,1.0]])],"derivedFrom":subQ0}),1.0]])]});}
            var Q17;
            {var subQ0=sQuery(id+"F25.wireOp",EDGE,"E65.54.0");var subQ1=makeQuery(id+"F24.opExtrude","CAP_EDGE",EDGE,{"disambiguationData":[OSD([sQuery(id+"F23.wireOp",EDGE,"E44")])],"isStart":false});var subQ2=makeQuery(id+"F25.imprint","INTERSECT",VERTEX,{"disambiguationData":[OD(0.0)],"derivedFrom":[subQ1,subQ0]});Q17=makeQuery(id+"F25.imprint","IMPRINT",FACE,{"disambiguationData":[TD([[makeQuery(id+"F25.imprint","IMPRINT",EDGE,{"disambiguationData":[TD([[subQ2,-1.0]])],"derivedFrom":subQ0}),1.0]])]});}
            var Q18;
            {var subQ0=sQuery(id+"F25.wireOp",EDGE,"E65.53.0");var subQ1=makeQuery(id+"F24.opExtrude","CAP_EDGE",EDGE,{"disambiguationData":[OSD([sQuery(id+"F23.wireOp",EDGE,"E44")])],"isStart":false});var subQ2=makeQuery(id+"F25.imprint","INTERSECT",VERTEX,{"disambiguationData":[OD(0.0)],"derivedFrom":[subQ1,subQ0]});Q18=makeQuery(id+"F25.imprint","IMPRINT",FACE,{"disambiguationData":[TD([[makeQuery(id+"F25.imprint","IMPRINT",EDGE,{"disambiguationData":[TD([[subQ2,-1.0]])],"derivedFrom":subQ0}),1.0]])]});}
            var Q19;
            {var subQ0=sQuery(id+"F25.wireOp",EDGE,"E65.53.0");var subQ1=makeQuery(id+"F24.opExtrude","CAP_EDGE",EDGE,{"disambiguationData":[OSD([sQuery(id+"F23.wireOp",EDGE,"E44")])],"isStart":false});var subQ2=makeQuery(id+"F25.imprint","INTERSECT",VERTEX,{"disambiguationData":[OD(0.0)],"derivedFrom":[subQ1,subQ0]});Q19=makeQuery(id+"F25.imprint","IMPRINT",FACE,{"disambiguationData":[TD([[makeQuery(id+"F25.imprint","IMPRINT",EDGE,{"disambiguationData":[TD([[subQ2,1.0]])],"derivedFrom":subQ0}),1.0]])]});}
            var Q20;
            {var subQ0=sQuery(id+"F25.wireOp",EDGE,"E65.52.0");var subQ1=makeQuery(id+"F24.opExtrude","CAP_EDGE",EDGE,{"disambiguationData":[OSD([sQuery(id+"F23.wireOp",EDGE,"E44")])],"isStart":false});var subQ2=makeQuery(id+"F25.imprint","INTERSECT",VERTEX,{"disambiguationData":[OD(0.0)],"derivedFrom":[subQ1,subQ0]});Q20=makeQuery(id+"F25.imprint","IMPRINT",FACE,{"disambiguationData":[TD([[makeQuery(id+"F25.imprint","IMPRINT",EDGE,{"disambiguationData":[TD([[subQ2,1.0]])],"derivedFrom":subQ0}),1.0]])]});}
            var Q21;
            {var subQ0=sQuery(id+"F25.wireOp",EDGE,"E65.52.0");var subQ1=makeQuery(id+"F24.opExtrude","CAP_EDGE",EDGE,{"disambiguationData":[OSD([sQuery(id+"F23.wireOp",EDGE,"E44")])],"isStart":false});var subQ2=makeQuery(id+"F25.imprint","INTERSECT",VERTEX,{"disambiguationData":[OD(0.0)],"derivedFrom":[subQ1,subQ0]});Q21=makeQuery(id+"F25.imprint","IMPRINT",FACE,{"disambiguationData":[TD([[makeQuery(id+"F25.imprint","IMPRINT",EDGE,{"disambiguationData":[TD([[subQ2,-1.0]])],"derivedFrom":subQ0}),1.0]])]});}
            var Q22;
            {var subQ0=sQuery(id+"F25.wireOp",EDGE,"E65.51.0");var subQ1=makeQuery(id+"F24.opExtrude","CAP_EDGE",EDGE,{"disambiguationData":[OSD([sQuery(id+"F23.wireOp",EDGE,"E44")])],"isStart":false});var subQ2=makeQuery(id+"F25.imprint","INTERSECT",VERTEX,{"disambiguationData":[OD(0.0)],"derivedFrom":[subQ1,subQ0]});Q22=makeQuery(id+"F25.imprint","IMPRINT",FACE,{"disambiguationData":[TD([[makeQuery(id+"F25.imprint","IMPRINT",EDGE,{"disambiguationData":[TD([[subQ2,-1.0]])],"derivedFrom":subQ0}),1.0]])]});}
            var Q23;
            {var subQ0=sQuery(id+"F25.wireOp",EDGE,"E65.51.0");var subQ1=makeQuery(id+"F24.opExtrude","CAP_EDGE",EDGE,{"disambiguationData":[OSD([sQuery(id+"F23.wireOp",EDGE,"E44")])],"isStart":false});var subQ2=makeQuery(id+"F25.imprint","INTERSECT",VERTEX,{"disambiguationData":[OD(0.0)],"derivedFrom":[subQ1,subQ0]});Q23=makeQuery(id+"F25.imprint","IMPRINT",FACE,{"disambiguationData":[TD([[makeQuery(id+"F25.imprint","IMPRINT",EDGE,{"disambiguationData":[TD([[subQ2,1.0]])],"derivedFrom":subQ0}),1.0]])]});}
            var Q24;
            {var subQ0=sQuery(id+"F25.wireOp",EDGE,"E65.50.0");var subQ1=makeQuery(id+"F24.opExtrude","CAP_EDGE",EDGE,{"disambiguationData":[OSD([sQuery(id+"F23.wireOp",EDGE,"E44")])],"isStart":false});var subQ2=makeQuery(id+"F25.imprint","INTERSECT",VERTEX,{"disambiguationData":[OD(0.0)],"derivedFrom":[subQ1,subQ0]});Q24=makeQuery(id+"F25.imprint","IMPRINT",FACE,{"disambiguationData":[TD([[makeQuery(id+"F25.imprint","IMPRINT",EDGE,{"disambiguationData":[TD([[subQ2,1.0]])],"derivedFrom":subQ0}),1.0]])]});}
            var Q25;
            {var subQ0=sQuery(id+"F25.wireOp",EDGE,"E65.50.0");var subQ1=makeQuery(id+"F24.opExtrude","CAP_EDGE",EDGE,{"disambiguationData":[OSD([sQuery(id+"F23.wireOp",EDGE,"E44")])],"isStart":false});var subQ2=makeQuery(id+"F25.imprint","INTERSECT",VERTEX,{"disambiguationData":[OD(0.0)],"derivedFrom":[subQ1,subQ0]});Q25=makeQuery(id+"F25.imprint","IMPRINT",FACE,{"disambiguationData":[TD([[makeQuery(id+"F25.imprint","IMPRINT",EDGE,{"disambiguationData":[TD([[subQ2,-1.0]])],"derivedFrom":subQ0}),1.0]])]});}
            var Q26;
            {var subQ0=sQuery(id+"F25.wireOp",EDGE,"E65.49.0");var subQ1=makeQuery(id+"F24.opExtrude","CAP_EDGE",EDGE,{"disambiguationData":[OSD([sQuery(id+"F23.wireOp",EDGE,"E44")])],"isStart":false});var subQ2=makeQuery(id+"F25.imprint","INTERSECT",VERTEX,{"disambiguationData":[OD(0.0)],"derivedFrom":[subQ1,subQ0]});Q26=makeQuery(id+"F25.imprint","IMPRINT",FACE,{"disambiguationData":[TD([[makeQuery(id+"F25.imprint","IMPRINT",EDGE,{"disambiguationData":[TD([[subQ2,-1.0]])],"derivedFrom":subQ0}),1.0]])]});}
            var Q27;
            {var subQ0=sQuery(id+"F25.wireOp",EDGE,"E65.49.0");var subQ1=makeQuery(id+"F24.opExtrude","CAP_EDGE",EDGE,{"disambiguationData":[OSD([sQuery(id+"F23.wireOp",EDGE,"E44")])],"isStart":false});var subQ2=makeQuery(id+"F25.imprint","INTERSECT",VERTEX,{"disambiguationData":[OD(0.0)],"derivedFrom":[subQ1,subQ0]});Q27=makeQuery(id+"F25.imprint","IMPRINT",FACE,{"disambiguationData":[TD([[makeQuery(id+"F25.imprint","IMPRINT",EDGE,{"disambiguationData":[TD([[subQ2,1.0]])],"derivedFrom":subQ0}),1.0]])]});}
            var Q28;
            {var subQ0=sQuery(id+"F25.wireOp",EDGE,"E65.48.0");var subQ1=makeQuery(id+"F24.opExtrude","CAP_EDGE",EDGE,{"disambiguationData":[OSD([sQuery(id+"F23.wireOp",EDGE,"E44")])],"isStart":false});var subQ2=makeQuery(id+"F25.imprint","INTERSECT",VERTEX,{"disambiguationData":[OD(0.0)],"derivedFrom":[subQ1,subQ0]});Q28=makeQuery(id+"F25.imprint","IMPRINT",FACE,{"disambiguationData":[TD([[makeQuery(id+"F25.imprint","IMPRINT",EDGE,{"disambiguationData":[TD([[subQ2,1.0]])],"derivedFrom":subQ0}),1.0]])]});}
            var Q29;
            {var subQ0=sQuery(id+"F25.wireOp",EDGE,"E65.48.0");var subQ1=makeQuery(id+"F24.opExtrude","CAP_EDGE",EDGE,{"disambiguationData":[OSD([sQuery(id+"F23.wireOp",EDGE,"E44")])],"isStart":false});var subQ2=makeQuery(id+"F25.imprint","INTERSECT",VERTEX,{"disambiguationData":[OD(0.0)],"derivedFrom":[subQ1,subQ0]});Q29=makeQuery(id+"F25.imprint","IMPRINT",FACE,{"disambiguationData":[TD([[makeQuery(id+"F25.imprint","IMPRINT",EDGE,{"disambiguationData":[TD([[subQ2,-1.0]])],"derivedFrom":subQ0}),1.0]])]});}
            var Q30;
            {var subQ0=sQuery(id+"F25.wireOp",EDGE,"E65.47.0");var subQ1=makeQuery(id+"F24.opExtrude","CAP_EDGE",EDGE,{"disambiguationData":[OSD([sQuery(id+"F23.wireOp",EDGE,"E44")])],"isStart":false});var subQ2=makeQuery(id+"F25.imprint","INTERSECT",VERTEX,{"disambiguationData":[OD(0.0)],"derivedFrom":[subQ1,subQ0]});Q30=makeQuery(id+"F25.imprint","IMPRINT",FACE,{"disambiguationData":[TD([[makeQuery(id+"F25.imprint","IMPRINT",EDGE,{"disambiguationData":[TD([[subQ2,-1.0]])],"derivedFrom":subQ0}),1.0]])]});}
            var Q31;
            {var subQ0=sQuery(id+"F25.wireOp",EDGE,"E65.47.0");var subQ1=makeQuery(id+"F24.opExtrude","CAP_EDGE",EDGE,{"disambiguationData":[OSD([sQuery(id+"F23.wireOp",EDGE,"E44")])],"isStart":false});var subQ2=makeQuery(id+"F25.imprint","INTERSECT",VERTEX,{"disambiguationData":[OD(0.0)],"derivedFrom":[subQ1,subQ0]});Q31=makeQuery(id+"F25.imprint","IMPRINT",FACE,{"disambiguationData":[TD([[makeQuery(id+"F25.imprint","IMPRINT",EDGE,{"disambiguationData":[TD([[subQ2,1.0]])],"derivedFrom":subQ0}),1.0]])]});}
            var Q32;
            {var subQ0=sQuery(id+"F25.wireOp",EDGE,"E65.46.0");var subQ1=makeQuery(id+"F24.opExtrude","CAP_EDGE",EDGE,{"disambiguationData":[OSD([sQuery(id+"F23.wireOp",EDGE,"E44")])],"isStart":false});var subQ2=makeQuery(id+"F25.imprint","INTERSECT",VERTEX,{"disambiguationData":[OD(0.0)],"derivedFrom":[subQ1,subQ0]});Q32=makeQuery(id+"F25.imprint","IMPRINT",FACE,{"disambiguationData":[TD([[makeQuery(id+"F25.imprint","IMPRINT",EDGE,{"disambiguationData":[TD([[subQ2,1.0]])],"derivedFrom":subQ0}),1.0]])]});}
            var Q33;
            {var subQ0=sQuery(id+"F25.wireOp",EDGE,"E65.46.0");var subQ1=makeQuery(id+"F24.opExtrude","CAP_EDGE",EDGE,{"disambiguationData":[OSD([sQuery(id+"F23.wireOp",EDGE,"E44")])],"isStart":false});var subQ2=makeQuery(id+"F25.imprint","INTERSECT",VERTEX,{"disambiguationData":[OD(0.0)],"derivedFrom":[subQ1,subQ0]});Q33=makeQuery(id+"F25.imprint","IMPRINT",FACE,{"disambiguationData":[TD([[makeQuery(id+"F25.imprint","IMPRINT",EDGE,{"disambiguationData":[TD([[subQ2,-1.0]])],"derivedFrom":subQ0}),1.0]])]});}
            var Q34;
            {var subQ0=sQuery(id+"F25.wireOp",EDGE,"E65.45.0");var subQ1=makeQuery(id+"F24.opExtrude","CAP_EDGE",EDGE,{"disambiguationData":[OSD([sQuery(id+"F23.wireOp",EDGE,"E44")])],"isStart":false});var subQ2=makeQuery(id+"F25.imprint","INTERSECT",VERTEX,{"disambiguationData":[OD(0.0)],"derivedFrom":[subQ1,subQ0]});Q34=makeQuery(id+"F25.imprint","IMPRINT",FACE,{"disambiguationData":[TD([[makeQuery(id+"F25.imprint","IMPRINT",EDGE,{"disambiguationData":[TD([[subQ2,1.0]])],"derivedFrom":subQ0}),1.0]])]});}
            var Q35;
            {var subQ0=sQuery(id+"F25.wireOp",EDGE,"E65.45.0");var subQ1=makeQuery(id+"F24.opExtrude","CAP_EDGE",EDGE,{"disambiguationData":[OSD([sQuery(id+"F23.wireOp",EDGE,"E44")])],"isStart":false});var subQ2=makeQuery(id+"F25.imprint","INTERSECT",VERTEX,{"disambiguationData":[OD(0.0)],"derivedFrom":[subQ1,subQ0]});Q35=makeQuery(id+"F25.imprint","IMPRINT",FACE,{"disambiguationData":[TD([[makeQuery(id+"F25.imprint","IMPRINT",EDGE,{"disambiguationData":[TD([[subQ2,-1.0]])],"derivedFrom":subQ0}),1.0]])]});}
            var Q36;
            {var subQ0=sQuery(id+"F25.wireOp",EDGE,"E65.44.0");var subQ1=makeQuery(id+"F24.opExtrude","CAP_EDGE",EDGE,{"disambiguationData":[OSD([sQuery(id+"F23.wireOp",EDGE,"E44")])],"isStart":false});var subQ2=makeQuery(id+"F25.imprint","INTERSECT",VERTEX,{"disambiguationData":[OD(0.0)],"derivedFrom":[subQ1,subQ0]});Q36=makeQuery(id+"F25.imprint","IMPRINT",FACE,{"disambiguationData":[TD([[makeQuery(id+"F25.imprint","IMPRINT",EDGE,{"disambiguationData":[TD([[subQ2,-1.0]])],"derivedFrom":subQ0}),1.0]])]});}
            var Q37;
            {var subQ0=sQuery(id+"F25.wireOp",EDGE,"E65.44.0");var subQ1=makeQuery(id+"F24.opExtrude","CAP_EDGE",EDGE,{"disambiguationData":[OSD([sQuery(id+"F23.wireOp",EDGE,"E44")])],"isStart":false});var subQ2=makeQuery(id+"F25.imprint","INTERSECT",VERTEX,{"disambiguationData":[OD(0.0)],"derivedFrom":[subQ1,subQ0]});Q37=makeQuery(id+"F25.imprint","IMPRINT",FACE,{"disambiguationData":[TD([[makeQuery(id+"F25.imprint","IMPRINT",EDGE,{"disambiguationData":[TD([[subQ2,1.0]])],"derivedFrom":subQ0}),1.0]])]});}
            var Q38;
            {var subQ0=sQuery(id+"F25.wireOp",EDGE,"E65.43.0");var subQ1=makeQuery(id+"F24.opExtrude","CAP_EDGE",EDGE,{"disambiguationData":[OSD([sQuery(id+"F23.wireOp",EDGE,"E44")])],"isStart":false});var subQ2=makeQuery(id+"F25.imprint","INTERSECT",VERTEX,{"disambiguationData":[OD(0.0)],"derivedFrom":[subQ1,subQ0]});Q38=makeQuery(id+"F25.imprint","IMPRINT",FACE,{"disambiguationData":[TD([[makeQuery(id+"F25.imprint","IMPRINT",EDGE,{"disambiguationData":[TD([[subQ2,1.0]])],"derivedFrom":subQ0}),1.0]])]});}
            var Q39;
            {var subQ0=sQuery(id+"F25.wireOp",EDGE,"E65.43.0");var subQ1=makeQuery(id+"F24.opExtrude","CAP_EDGE",EDGE,{"disambiguationData":[OSD([sQuery(id+"F23.wireOp",EDGE,"E44")])],"isStart":false});var subQ2=makeQuery(id+"F25.imprint","INTERSECT",VERTEX,{"disambiguationData":[OD(0.0)],"derivedFrom":[subQ1,subQ0]});Q39=makeQuery(id+"F25.imprint","IMPRINT",FACE,{"disambiguationData":[TD([[makeQuery(id+"F25.imprint","IMPRINT",EDGE,{"disambiguationData":[TD([[subQ2,-1.0]])],"derivedFrom":subQ0}),1.0]])]});}
            var Q40;
            {var subQ0=sQuery(id+"F25.wireOp",EDGE,"E65.42.0");var subQ1=makeQuery(id+"F24.opExtrude","CAP_EDGE",EDGE,{"disambiguationData":[OSD([sQuery(id+"F23.wireOp",EDGE,"E44")])],"isStart":false});var subQ2=makeQuery(id+"F25.imprint","INTERSECT",VERTEX,{"disambiguationData":[OD(0.0)],"derivedFrom":[subQ1,subQ0]});Q40=makeQuery(id+"F25.imprint","IMPRINT",FACE,{"disambiguationData":[TD([[makeQuery(id+"F25.imprint","IMPRINT",EDGE,{"disambiguationData":[TD([[subQ2,1.0]])],"derivedFrom":subQ0}),1.0]])]});}
            var Q41;
            {var subQ0=sQuery(id+"F25.wireOp",EDGE,"E65.42.0");var subQ1=makeQuery(id+"F24.opExtrude","CAP_EDGE",EDGE,{"disambiguationData":[OSD([sQuery(id+"F23.wireOp",EDGE,"E44")])],"isStart":false});var subQ2=makeQuery(id+"F25.imprint","INTERSECT",VERTEX,{"disambiguationData":[OD(0.0)],"derivedFrom":[subQ1,subQ0]});Q41=makeQuery(id+"F25.imprint","IMPRINT",FACE,{"disambiguationData":[TD([[makeQuery(id+"F25.imprint","IMPRINT",EDGE,{"disambiguationData":[TD([[subQ2,-1.0]])],"derivedFrom":subQ0}),1.0]])]});}
            var Q42;
            {var subQ0=sQuery(id+"F25.wireOp",EDGE,"E65.41.0");var subQ1=makeQuery(id+"F24.opExtrude","CAP_EDGE",EDGE,{"disambiguationData":[OSD([sQuery(id+"F23.wireOp",EDGE,"E44")])],"isStart":false});var subQ2=makeQuery(id+"F25.imprint","INTERSECT",VERTEX,{"disambiguationData":[OD(0.0)],"derivedFrom":[subQ1,subQ0]});Q42=makeQuery(id+"F25.imprint","IMPRINT",FACE,{"disambiguationData":[TD([[makeQuery(id+"F25.imprint","IMPRINT",EDGE,{"disambiguationData":[TD([[subQ2,1.0]])],"derivedFrom":subQ0}),1.0]])]});}
            var Q43;
            {var subQ0=sQuery(id+"F25.wireOp",EDGE,"E65.41.0");var subQ1=makeQuery(id+"F24.opExtrude","CAP_EDGE",EDGE,{"disambiguationData":[OSD([sQuery(id+"F23.wireOp",EDGE,"E44")])],"isStart":false});var subQ2=makeQuery(id+"F25.imprint","INTERSECT",VERTEX,{"disambiguationData":[OD(0.0)],"derivedFrom":[subQ1,subQ0]});Q43=makeQuery(id+"F25.imprint","IMPRINT",FACE,{"disambiguationData":[TD([[makeQuery(id+"F25.imprint","IMPRINT",EDGE,{"disambiguationData":[TD([[subQ2,-1.0]])],"derivedFrom":subQ0}),1.0]])]});}
            var Q44;
            {var subQ0=sQuery(id+"F25.wireOp",EDGE,"E65.40.0");var subQ1=makeQuery(id+"F24.opExtrude","CAP_EDGE",EDGE,{"disambiguationData":[OSD([sQuery(id+"F23.wireOp",EDGE,"E44")])],"isStart":false});var subQ2=makeQuery(id+"F25.imprint","INTERSECT",VERTEX,{"disambiguationData":[OD(0.0)],"derivedFrom":[subQ1,subQ0]});Q44=makeQuery(id+"F25.imprint","IMPRINT",FACE,{"disambiguationData":[TD([[makeQuery(id+"F25.imprint","IMPRINT",EDGE,{"disambiguationData":[TD([[subQ2,1.0]])],"derivedFrom":subQ0}),1.0]])]});}
            var Q45;
            {var subQ0=sQuery(id+"F25.wireOp",EDGE,"E65.40.0");var subQ1=makeQuery(id+"F24.opExtrude","CAP_EDGE",EDGE,{"disambiguationData":[OSD([sQuery(id+"F23.wireOp",EDGE,"E44")])],"isStart":false});var subQ2=makeQuery(id+"F25.imprint","INTERSECT",VERTEX,{"disambiguationData":[OD(0.0)],"derivedFrom":[subQ1,subQ0]});Q45=makeQuery(id+"F25.imprint","IMPRINT",FACE,{"disambiguationData":[TD([[makeQuery(id+"F25.imprint","IMPRINT",EDGE,{"disambiguationData":[TD([[subQ2,-1.0]])],"derivedFrom":subQ0}),1.0]])]});}
            var Q46;
            {var subQ0=sQuery(id+"F25.wireOp",EDGE,"E65.39.0");var subQ1=makeQuery(id+"F24.opExtrude","CAP_EDGE",EDGE,{"disambiguationData":[OSD([sQuery(id+"F23.wireOp",EDGE,"E44")])],"isStart":false});var subQ2=makeQuery(id+"F25.imprint","INTERSECT",VERTEX,{"disambiguationData":[OD(0.0)],"derivedFrom":[subQ1,subQ0]});Q46=makeQuery(id+"F25.imprint","IMPRINT",FACE,{"disambiguationData":[TD([[makeQuery(id+"F25.imprint","IMPRINT",EDGE,{"disambiguationData":[TD([[subQ2,1.0]])],"derivedFrom":subQ0}),1.0]])]});}
            var Q47;
            {var subQ0=sQuery(id+"F25.wireOp",EDGE,"E65.39.0");var subQ1=makeQuery(id+"F24.opExtrude","CAP_EDGE",EDGE,{"disambiguationData":[OSD([sQuery(id+"F23.wireOp",EDGE,"E44")])],"isStart":false});var subQ2=makeQuery(id+"F25.imprint","INTERSECT",VERTEX,{"disambiguationData":[OD(0.0)],"derivedFrom":[subQ1,subQ0]});Q47=makeQuery(id+"F25.imprint","IMPRINT",FACE,{"disambiguationData":[TD([[makeQuery(id+"F25.imprint","IMPRINT",EDGE,{"disambiguationData":[TD([[subQ2,-1.0]])],"derivedFrom":subQ0}),1.0]])]});}
            var Q48;
            {var subQ0=sQuery(id+"F25.wireOp",EDGE,"E65.38.0");var subQ1=makeQuery(id+"F24.opExtrude","CAP_EDGE",EDGE,{"disambiguationData":[OSD([sQuery(id+"F23.wireOp",EDGE,"E44")])],"isStart":false});var subQ2=makeQuery(id+"F25.imprint","INTERSECT",VERTEX,{"disambiguationData":[OD(0.0)],"derivedFrom":[subQ1,subQ0]});Q48=makeQuery(id+"F25.imprint","IMPRINT",FACE,{"disambiguationData":[TD([[makeQuery(id+"F25.imprint","IMPRINT",EDGE,{"disambiguationData":[TD([[subQ2,-1.0]])],"derivedFrom":subQ0}),1.0]])]});}
            var Q49;
            {var subQ0=sQuery(id+"F25.wireOp",EDGE,"E65.38.0");var subQ1=makeQuery(id+"F24.opExtrude","CAP_EDGE",EDGE,{"disambiguationData":[OSD([sQuery(id+"F23.wireOp",EDGE,"E44")])],"isStart":false});var subQ2=makeQuery(id+"F25.imprint","INTERSECT",VERTEX,{"disambiguationData":[OD(0.0)],"derivedFrom":[subQ1,subQ0]});Q49=makeQuery(id+"F25.imprint","IMPRINT",FACE,{"disambiguationData":[TD([[makeQuery(id+"F25.imprint","IMPRINT",EDGE,{"disambiguationData":[TD([[subQ2,1.0]])],"derivedFrom":subQ0}),1.0]])]});}
            var Q50;
            {var subQ0=sQuery(id+"F25.wireOp",EDGE,"E65.37.0");var subQ1=makeQuery(id+"F24.opExtrude","CAP_EDGE",EDGE,{"disambiguationData":[OSD([sQuery(id+"F23.wireOp",EDGE,"E44")])],"isStart":false});var subQ2=makeQuery(id+"F25.imprint","INTERSECT",VERTEX,{"disambiguationData":[OD(0.0)],"derivedFrom":[subQ1,subQ0]});Q50=makeQuery(id+"F25.imprint","IMPRINT",FACE,{"disambiguationData":[TD([[makeQuery(id+"F25.imprint","IMPRINT",EDGE,{"disambiguationData":[TD([[subQ2,1.0]])],"derivedFrom":subQ0}),1.0]])]});}
            var Q51;
            {var subQ0=sQuery(id+"F25.wireOp",EDGE,"E65.37.0");var subQ1=makeQuery(id+"F24.opExtrude","CAP_EDGE",EDGE,{"disambiguationData":[OSD([sQuery(id+"F23.wireOp",EDGE,"E44")])],"isStart":false});var subQ2=makeQuery(id+"F25.imprint","INTERSECT",VERTEX,{"disambiguationData":[OD(0.0)],"derivedFrom":[subQ1,subQ0]});Q51=makeQuery(id+"F25.imprint","IMPRINT",FACE,{"disambiguationData":[TD([[makeQuery(id+"F25.imprint","IMPRINT",EDGE,{"disambiguationData":[TD([[subQ2,-1.0]])],"derivedFrom":subQ0}),1.0]])]});}
            var Q52;
            {var subQ0=sQuery(id+"F25.wireOp",EDGE,"E65.36.0");var subQ1=makeQuery(id+"F24.opExtrude","CAP_EDGE",EDGE,{"disambiguationData":[OSD([sQuery(id+"F23.wireOp",EDGE,"E44")])],"isStart":false});var subQ2=makeQuery(id+"F25.imprint","INTERSECT",VERTEX,{"disambiguationData":[OD(0.0)],"derivedFrom":[subQ1,subQ0]});Q52=makeQuery(id+"F25.imprint","IMPRINT",FACE,{"disambiguationData":[TD([[makeQuery(id+"F25.imprint","IMPRINT",EDGE,{"disambiguationData":[TD([[subQ2,1.0]])],"derivedFrom":subQ0}),1.0]])]});}
            var Q53;
            {var subQ0=sQuery(id+"F25.wireOp",EDGE,"E65.36.0");var subQ1=makeQuery(id+"F24.opExtrude","CAP_EDGE",EDGE,{"disambiguationData":[OSD([sQuery(id+"F23.wireOp",EDGE,"E44")])],"isStart":false});var subQ2=makeQuery(id+"F25.imprint","INTERSECT",VERTEX,{"disambiguationData":[OD(0.0)],"derivedFrom":[subQ1,subQ0]});Q53=makeQuery(id+"F25.imprint","IMPRINT",FACE,{"disambiguationData":[TD([[makeQuery(id+"F25.imprint","IMPRINT",EDGE,{"disambiguationData":[TD([[subQ2,-1.0]])],"derivedFrom":subQ0}),1.0]])]});}
            var Q54;
            {var subQ0=sQuery(id+"F25.wireOp",EDGE,"E65.35.0");var subQ1=makeQuery(id+"F24.opExtrude","CAP_EDGE",EDGE,{"disambiguationData":[OSD([sQuery(id+"F23.wireOp",EDGE,"E44")])],"isStart":false});var subQ2=makeQuery(id+"F25.imprint","INTERSECT",VERTEX,{"disambiguationData":[OD(0.0)],"derivedFrom":[subQ1,subQ0]});Q54=makeQuery(id+"F25.imprint","IMPRINT",FACE,{"disambiguationData":[TD([[makeQuery(id+"F25.imprint","IMPRINT",EDGE,{"disambiguationData":[TD([[subQ2,-1.0]])],"derivedFrom":subQ0}),1.0]])]});}
            var Q55;
            {var subQ0=sQuery(id+"F25.wireOp",EDGE,"E65.35.0");var subQ1=makeQuery(id+"F24.opExtrude","CAP_EDGE",EDGE,{"disambiguationData":[OSD([sQuery(id+"F23.wireOp",EDGE,"E44")])],"isStart":false});var subQ2=makeQuery(id+"F25.imprint","INTERSECT",VERTEX,{"disambiguationData":[OD(0.0)],"derivedFrom":[subQ1,subQ0]});Q55=makeQuery(id+"F25.imprint","IMPRINT",FACE,{"disambiguationData":[TD([[makeQuery(id+"F25.imprint","IMPRINT",EDGE,{"disambiguationData":[TD([[subQ2,1.0]])],"derivedFrom":subQ0}),1.0]])]});}
            var Q56;
            {var subQ0=sQuery(id+"F25.wireOp",EDGE,"E65.34.0");var subQ1=makeQuery(id+"F24.opExtrude","CAP_EDGE",EDGE,{"disambiguationData":[OSD([sQuery(id+"F23.wireOp",EDGE,"E44")])],"isStart":false});var subQ2=makeQuery(id+"F25.imprint","INTERSECT",VERTEX,{"disambiguationData":[OD(0.0)],"derivedFrom":[subQ1,subQ0]});Q56=makeQuery(id+"F25.imprint","IMPRINT",FACE,{"disambiguationData":[TD([[makeQuery(id+"F25.imprint","IMPRINT",EDGE,{"disambiguationData":[TD([[subQ2,1.0]])],"derivedFrom":subQ0}),1.0]])]});}
            var Q57;
            {var subQ0=sQuery(id+"F25.wireOp",EDGE,"E65.34.0");var subQ1=makeQuery(id+"F24.opExtrude","CAP_EDGE",EDGE,{"disambiguationData":[OSD([sQuery(id+"F23.wireOp",EDGE,"E44")])],"isStart":false});var subQ2=makeQuery(id+"F25.imprint","INTERSECT",VERTEX,{"disambiguationData":[OD(0.0)],"derivedFrom":[subQ1,subQ0]});Q57=makeQuery(id+"F25.imprint","IMPRINT",FACE,{"disambiguationData":[TD([[makeQuery(id+"F25.imprint","IMPRINT",EDGE,{"disambiguationData":[TD([[subQ2,-1.0]])],"derivedFrom":subQ0}),1.0]])]});}
            var Q58;
            {var subQ0=sQuery(id+"F25.wireOp",EDGE,"E65.33.0");var subQ1=makeQuery(id+"F24.opExtrude","CAP_EDGE",EDGE,{"disambiguationData":[OSD([sQuery(id+"F23.wireOp",EDGE,"E44")])],"isStart":false});var subQ2=makeQuery(id+"F25.imprint","INTERSECT",VERTEX,{"disambiguationData":[OD(0.0)],"derivedFrom":[subQ1,subQ0]});Q58=makeQuery(id+"F25.imprint","IMPRINT",FACE,{"disambiguationData":[TD([[makeQuery(id+"F25.imprint","IMPRINT",EDGE,{"disambiguationData":[TD([[subQ2,1.0]])],"derivedFrom":subQ0}),1.0]])]});}
            var Q59;
            {var subQ0=sQuery(id+"F25.wireOp",EDGE,"E65.33.0");var subQ1=makeQuery(id+"F24.opExtrude","CAP_EDGE",EDGE,{"disambiguationData":[OSD([sQuery(id+"F23.wireOp",EDGE,"E44")])],"isStart":false});var subQ2=makeQuery(id+"F25.imprint","INTERSECT",VERTEX,{"disambiguationData":[OD(0.0)],"derivedFrom":[subQ1,subQ0]});Q59=makeQuery(id+"F25.imprint","IMPRINT",FACE,{"disambiguationData":[TD([[makeQuery(id+"F25.imprint","IMPRINT",EDGE,{"disambiguationData":[TD([[subQ2,-1.0]])],"derivedFrom":subQ0}),1.0]])]});}
            var Q60;
            {var subQ0=sQuery(id+"F25.wireOp",EDGE,"E65.32.0");var subQ1=makeQuery(id+"F24.opExtrude","CAP_EDGE",EDGE,{"disambiguationData":[OSD([sQuery(id+"F23.wireOp",EDGE,"E44")])],"isStart":false});var subQ2=makeQuery(id+"F25.imprint","INTERSECT",VERTEX,{"disambiguationData":[OD(0.0)],"derivedFrom":[subQ1,subQ0]});Q60=makeQuery(id+"F25.imprint","IMPRINT",FACE,{"disambiguationData":[TD([[makeQuery(id+"F25.imprint","IMPRINT",EDGE,{"disambiguationData":[TD([[subQ2,1.0]])],"derivedFrom":subQ0}),1.0]])]});}
            var Q61;
            {var subQ0=sQuery(id+"F25.wireOp",EDGE,"E65.32.0");var subQ1=makeQuery(id+"F24.opExtrude","CAP_EDGE",EDGE,{"disambiguationData":[OSD([sQuery(id+"F23.wireOp",EDGE,"E44")])],"isStart":false});var subQ2=makeQuery(id+"F25.imprint","INTERSECT",VERTEX,{"disambiguationData":[OD(0.0)],"derivedFrom":[subQ1,subQ0]});Q61=makeQuery(id+"F25.imprint","IMPRINT",FACE,{"disambiguationData":[TD([[makeQuery(id+"F25.imprint","IMPRINT",EDGE,{"disambiguationData":[TD([[subQ2,-1.0]])],"derivedFrom":subQ0}),1.0]])]});}
            var Q62;
            {var subQ0=sQuery(id+"F25.wireOp",EDGE,"E65.31.0");var subQ1=makeQuery(id+"F24.opExtrude","CAP_EDGE",EDGE,{"disambiguationData":[OSD([sQuery(id+"F23.wireOp",EDGE,"E44")])],"isStart":false});var subQ2=makeQuery(id+"F25.imprint","INTERSECT",VERTEX,{"disambiguationData":[OD(0.0)],"derivedFrom":[subQ1,subQ0]});Q62=makeQuery(id+"F25.imprint","IMPRINT",FACE,{"disambiguationData":[TD([[makeQuery(id+"F25.imprint","IMPRINT",EDGE,{"disambiguationData":[TD([[subQ2,-1.0]])],"derivedFrom":subQ0}),1.0]])]});}
            var Q63;
            {var subQ0=sQuery(id+"F25.wireOp",EDGE,"E65.31.0");var subQ1=makeQuery(id+"F24.opExtrude","CAP_EDGE",EDGE,{"disambiguationData":[OSD([sQuery(id+"F23.wireOp",EDGE,"E44")])],"isStart":false});var subQ2=makeQuery(id+"F25.imprint","INTERSECT",VERTEX,{"disambiguationData":[OD(0.0)],"derivedFrom":[subQ1,subQ0]});Q63=makeQuery(id+"F25.imprint","IMPRINT",FACE,{"disambiguationData":[TD([[makeQuery(id+"F25.imprint","IMPRINT",EDGE,{"disambiguationData":[TD([[subQ2,1.0]])],"derivedFrom":subQ0}),1.0]])]});}
            var Q64;
            {var subQ0=sQuery(id+"F25.wireOp",EDGE,"E65.30.0");var subQ1=sQuery(id+"F25.wireOp",EDGE,"E61");var subQ2=makeQuery(id+"F25.imprint","INTERSECT",VERTEX,{"disambiguationData":[OD(1.0)],"derivedFrom":[subQ1,subQ0]});Q64=makeQuery(id+"F25.imprint","IMPRINT",FACE,{"disambiguationData":[TD([[makeQuery(id+"F25.imprint","IMPRINT",EDGE,{"disambiguationData":[TD([[subQ2,1.0]])],"derivedFrom":subQ0}),1.0]])]});}
            var Q65;
            {var subQ0=sQuery(id+"F25.wireOp",EDGE,"E65.30.0");var subQ1=makeQuery(id+"F24.opExtrude","CAP_EDGE",EDGE,{"disambiguationData":[OSD([sQuery(id+"F23.wireOp",EDGE,"E44")])],"isStart":false});var subQ2=makeQuery(id+"F25.imprint","INTERSECT",VERTEX,{"disambiguationData":[OD(0.0)],"derivedFrom":[subQ1,subQ0]});Q65=makeQuery(id+"F25.imprint","IMPRINT",FACE,{"disambiguationData":[TD([[makeQuery(id+"F25.imprint","IMPRINT",EDGE,{"disambiguationData":[TD([[subQ2,1.0]])],"derivedFrom":subQ0}),1.0]])]});}
            var Q66;
            {var subQ0=sQuery(id+"F25.wireOp",EDGE,"E65.29.0");var subQ1=sQuery(id+"F25.wireOp",EDGE,"E61");var subQ2=makeQuery(id+"F25.imprint","INTERSECT",VERTEX,{"disambiguationData":[OD(0.0)],"derivedFrom":[subQ1,subQ0]});Q66=makeQuery(id+"F25.imprint","IMPRINT",FACE,{"disambiguationData":[TD([[makeQuery(id+"F25.imprint","IMPRINT",EDGE,{"disambiguationData":[TD([[subQ2,1.0]])],"derivedFrom":subQ0}),1.0]])]});}
            var Q67;
            {var subQ0=sQuery(id+"F25.wireOp",EDGE,"E65.29.0");var subQ1=makeQuery(id+"F24.opExtrude","CAP_EDGE",EDGE,{"disambiguationData":[OSD([sQuery(id+"F23.wireOp",EDGE,"E44")])],"isStart":false});var subQ2=makeQuery(id+"F25.imprint","INTERSECT",VERTEX,{"disambiguationData":[OD(0.0)],"derivedFrom":[subQ1,subQ0]});Q67=makeQuery(id+"F25.imprint","IMPRINT",FACE,{"disambiguationData":[TD([[makeQuery(id+"F25.imprint","IMPRINT",EDGE,{"disambiguationData":[TD([[subQ2,1.0]])],"derivedFrom":subQ0}),1.0]])]});}
            var Q68;
            {var subQ0=sQuery(id+"F25.wireOp",EDGE,"E65.28.0");var subQ1=makeQuery(id+"F24.opExtrude","CAP_EDGE",EDGE,{"disambiguationData":[OSD([sQuery(id+"F23.wireOp",EDGE,"E44")])],"isStart":false});var subQ2=makeQuery(id+"F25.imprint","INTERSECT",VERTEX,{"disambiguationData":[OD(0.0)],"derivedFrom":[subQ1,subQ0]});Q68=makeQuery(id+"F25.imprint","IMPRINT",FACE,{"disambiguationData":[TD([[makeQuery(id+"F25.imprint","IMPRINT",EDGE,{"disambiguationData":[TD([[subQ2,-1.0]])],"derivedFrom":subQ0}),1.0]])]});}
            var Q69;
            {var subQ0=sQuery(id+"F25.wireOp",EDGE,"E65.28.0");var subQ1=makeQuery(id+"F24.opExtrude","CAP_EDGE",EDGE,{"disambiguationData":[OSD([sQuery(id+"F23.wireOp",EDGE,"E44")])],"isStart":false});var subQ2=makeQuery(id+"F25.imprint","INTERSECT",VERTEX,{"disambiguationData":[OD(0.0)],"derivedFrom":[subQ1,subQ0]});Q69=makeQuery(id+"F25.imprint","IMPRINT",FACE,{"disambiguationData":[TD([[makeQuery(id+"F25.imprint","IMPRINT",EDGE,{"disambiguationData":[TD([[subQ2,1.0]])],"derivedFrom":subQ0}),1.0]])]});}
            var Q70;
            {var subQ0=sQuery(id+"F25.wireOp",EDGE,"E65.27.0");var subQ1=makeQuery(id+"F24.opExtrude","CAP_EDGE",EDGE,{"disambiguationData":[OSD([sQuery(id+"F23.wireOp",EDGE,"E44")])],"isStart":false});var subQ2=makeQuery(id+"F25.imprint","INTERSECT",VERTEX,{"disambiguationData":[OD(0.0)],"derivedFrom":[subQ1,subQ0]});Q70=makeQuery(id+"F25.imprint","IMPRINT",FACE,{"disambiguationData":[TD([[makeQuery(id+"F25.imprint","IMPRINT",EDGE,{"disambiguationData":[TD([[subQ2,-1.0]])],"derivedFrom":subQ0}),1.0]])]});}
            var Q71;
            {var subQ0=sQuery(id+"F25.wireOp",EDGE,"E65.27.0");var subQ1=makeQuery(id+"F24.opExtrude","CAP_EDGE",EDGE,{"disambiguationData":[OSD([sQuery(id+"F23.wireOp",EDGE,"E44")])],"isStart":false});var subQ2=makeQuery(id+"F25.imprint","INTERSECT",VERTEX,{"disambiguationData":[OD(0.0)],"derivedFrom":[subQ1,subQ0]});Q71=makeQuery(id+"F25.imprint","IMPRINT",FACE,{"disambiguationData":[TD([[makeQuery(id+"F25.imprint","IMPRINT",EDGE,{"disambiguationData":[TD([[subQ2,1.0]])],"derivedFrom":subQ0}),1.0]])]});}
            var Q72;
            {var subQ0=sQuery(id+"F25.wireOp",EDGE,"E65.26.0");var subQ1=makeQuery(id+"F24.opExtrude","CAP_EDGE",EDGE,{"disambiguationData":[OSD([sQuery(id+"F23.wireOp",EDGE,"E44")])],"isStart":false});var subQ2=makeQuery(id+"F25.imprint","INTERSECT",VERTEX,{"disambiguationData":[OD(0.0)],"derivedFrom":[subQ1,subQ0]});Q72=makeQuery(id+"F25.imprint","IMPRINT",FACE,{"disambiguationData":[TD([[makeQuery(id+"F25.imprint","IMPRINT",EDGE,{"disambiguationData":[TD([[subQ2,-1.0]])],"derivedFrom":subQ0}),1.0]])]});}
            var Q73;
            {var subQ0=sQuery(id+"F25.wireOp",EDGE,"E65.26.0");var subQ1=makeQuery(id+"F24.opExtrude","CAP_EDGE",EDGE,{"disambiguationData":[OSD([sQuery(id+"F23.wireOp",EDGE,"E44")])],"isStart":false});var subQ2=makeQuery(id+"F25.imprint","INTERSECT",VERTEX,{"disambiguationData":[OD(0.0)],"derivedFrom":[subQ1,subQ0]});Q73=makeQuery(id+"F25.imprint","IMPRINT",FACE,{"disambiguationData":[TD([[makeQuery(id+"F25.imprint","IMPRINT",EDGE,{"disambiguationData":[TD([[subQ2,1.0]])],"derivedFrom":subQ0}),1.0]])]});}
            var Q74;
            {var subQ0=sQuery(id+"F25.wireOp",EDGE,"E65.25.0");var subQ1=makeQuery(id+"F24.opExtrude","CAP_EDGE",EDGE,{"disambiguationData":[OSD([sQuery(id+"F23.wireOp",EDGE,"E44")])],"isStart":false});var subQ2=makeQuery(id+"F25.imprint","INTERSECT",VERTEX,{"disambiguationData":[OD(0.0)],"derivedFrom":[subQ1,subQ0]});Q74=makeQuery(id+"F25.imprint","IMPRINT",FACE,{"disambiguationData":[TD([[makeQuery(id+"F25.imprint","IMPRINT",EDGE,{"disambiguationData":[TD([[subQ2,-1.0]])],"derivedFrom":subQ0}),1.0]])]});}
            var Q75;
            {var subQ0=sQuery(id+"F25.wireOp",EDGE,"E65.25.0");var subQ1=makeQuery(id+"F24.opExtrude","CAP_EDGE",EDGE,{"disambiguationData":[OSD([sQuery(id+"F23.wireOp",EDGE,"E44")])],"isStart":false});var subQ2=makeQuery(id+"F25.imprint","INTERSECT",VERTEX,{"disambiguationData":[OD(0.0)],"derivedFrom":[subQ1,subQ0]});Q75=makeQuery(id+"F25.imprint","IMPRINT",FACE,{"disambiguationData":[TD([[makeQuery(id+"F25.imprint","IMPRINT",EDGE,{"disambiguationData":[TD([[subQ2,1.0]])],"derivedFrom":subQ0}),1.0]])]});}
            var Q76;
            {var subQ0=sQuery(id+"F25.wireOp",EDGE,"E65.24.0");var subQ1=makeQuery(id+"F24.opExtrude","CAP_EDGE",EDGE,{"disambiguationData":[OSD([sQuery(id+"F23.wireOp",EDGE,"E44")])],"isStart":false});var subQ2=makeQuery(id+"F25.imprint","INTERSECT",VERTEX,{"disambiguationData":[OD(0.0)],"derivedFrom":[subQ1,subQ0]});Q76=makeQuery(id+"F25.imprint","IMPRINT",FACE,{"disambiguationData":[TD([[makeQuery(id+"F25.imprint","IMPRINT",EDGE,{"disambiguationData":[TD([[subQ2,-1.0]])],"derivedFrom":subQ0}),1.0]])]});}
            var Q77;
            {var subQ0=sQuery(id+"F25.wireOp",EDGE,"E65.24.0");var subQ1=makeQuery(id+"F24.opExtrude","CAP_EDGE",EDGE,{"disambiguationData":[OSD([sQuery(id+"F23.wireOp",EDGE,"E44")])],"isStart":false});var subQ2=makeQuery(id+"F25.imprint","INTERSECT",VERTEX,{"disambiguationData":[OD(0.0)],"derivedFrom":[subQ1,subQ0]});Q77=makeQuery(id+"F25.imprint","IMPRINT",FACE,{"disambiguationData":[TD([[makeQuery(id+"F25.imprint","IMPRINT",EDGE,{"disambiguationData":[TD([[subQ2,1.0]])],"derivedFrom":subQ0}),1.0]])]});}
            var Q78;
            {var subQ0=sQuery(id+"F25.wireOp",EDGE,"E65.23.0");var subQ1=makeQuery(id+"F24.opExtrude","CAP_EDGE",EDGE,{"disambiguationData":[OSD([sQuery(id+"F23.wireOp",EDGE,"E44")])],"isStart":false});var subQ2=makeQuery(id+"F25.imprint","INTERSECT",VERTEX,{"disambiguationData":[OD(0.0)],"derivedFrom":[subQ1,subQ0]});Q78=makeQuery(id+"F25.imprint","IMPRINT",FACE,{"disambiguationData":[TD([[makeQuery(id+"F25.imprint","IMPRINT",EDGE,{"disambiguationData":[TD([[subQ2,1.0]])],"derivedFrom":subQ0}),1.0]])]});}
            var Q79;
            {var subQ0=sQuery(id+"F25.wireOp",EDGE,"E65.23.0");var subQ1=makeQuery(id+"F24.opExtrude","CAP_EDGE",EDGE,{"disambiguationData":[OSD([sQuery(id+"F23.wireOp",EDGE,"E44")])],"isStart":false});var subQ2=makeQuery(id+"F25.imprint","INTERSECT",VERTEX,{"disambiguationData":[OD(0.0)],"derivedFrom":[subQ1,subQ0]});Q79=makeQuery(id+"F25.imprint","IMPRINT",FACE,{"disambiguationData":[TD([[makeQuery(id+"F25.imprint","IMPRINT",EDGE,{"disambiguationData":[TD([[subQ2,-1.0]])],"derivedFrom":subQ0}),1.0]])]});}
            var Q80;
            {var subQ0=sQuery(id+"F25.wireOp",EDGE,"E65.22.0");var subQ1=makeQuery(id+"F24.opExtrude","CAP_EDGE",EDGE,{"disambiguationData":[OSD([sQuery(id+"F23.wireOp",EDGE,"E44")])],"isStart":false});var subQ2=makeQuery(id+"F25.imprint","INTERSECT",VERTEX,{"disambiguationData":[OD(0.0)],"derivedFrom":[subQ1,subQ0]});Q80=makeQuery(id+"F25.imprint","IMPRINT",FACE,{"disambiguationData":[TD([[makeQuery(id+"F25.imprint","IMPRINT",EDGE,{"disambiguationData":[TD([[subQ2,-1.0]])],"derivedFrom":subQ0}),1.0]])]});}
            var Q81;
            {var subQ0=sQuery(id+"F25.wireOp",EDGE,"E65.22.0");var subQ1=makeQuery(id+"F24.opExtrude","CAP_EDGE",EDGE,{"disambiguationData":[OSD([sQuery(id+"F23.wireOp",EDGE,"E44")])],"isStart":false});var subQ2=makeQuery(id+"F25.imprint","INTERSECT",VERTEX,{"disambiguationData":[OD(0.0)],"derivedFrom":[subQ1,subQ0]});Q81=makeQuery(id+"F25.imprint","IMPRINT",FACE,{"disambiguationData":[TD([[makeQuery(id+"F25.imprint","IMPRINT",EDGE,{"disambiguationData":[TD([[subQ2,1.0]])],"derivedFrom":subQ0}),1.0]])]});}
            var Q82;
            {var subQ0=sQuery(id+"F25.wireOp",EDGE,"E65.21.0");var subQ1=makeQuery(id+"F24.opExtrude","CAP_EDGE",EDGE,{"disambiguationData":[OSD([sQuery(id+"F23.wireOp",EDGE,"E44")])],"isStart":false});var subQ2=makeQuery(id+"F25.imprint","INTERSECT",VERTEX,{"disambiguationData":[OD(0.0)],"derivedFrom":[subQ1,subQ0]});Q82=makeQuery(id+"F25.imprint","IMPRINT",FACE,{"disambiguationData":[TD([[makeQuery(id+"F25.imprint","IMPRINT",EDGE,{"disambiguationData":[TD([[subQ2,1.0]])],"derivedFrom":subQ0}),1.0]])]});}
            var Q83;
            {var subQ0=sQuery(id+"F25.wireOp",EDGE,"E65.21.0");var subQ1=makeQuery(id+"F24.opExtrude","CAP_EDGE",EDGE,{"disambiguationData":[OSD([sQuery(id+"F23.wireOp",EDGE,"E44")])],"isStart":false});var subQ2=makeQuery(id+"F25.imprint","INTERSECT",VERTEX,{"disambiguationData":[OD(0.0)],"derivedFrom":[subQ1,subQ0]});Q83=makeQuery(id+"F25.imprint","IMPRINT",FACE,{"disambiguationData":[TD([[makeQuery(id+"F25.imprint","IMPRINT",EDGE,{"disambiguationData":[TD([[subQ2,-1.0]])],"derivedFrom":subQ0}),1.0]])]});}
            var Q84;
            {var subQ0=sQuery(id+"F25.wireOp",EDGE,"E65.20.0");var subQ1=makeQuery(id+"F24.opExtrude","CAP_EDGE",EDGE,{"disambiguationData":[OSD([sQuery(id+"F23.wireOp",EDGE,"E44")])],"isStart":false});var subQ2=makeQuery(id+"F25.imprint","INTERSECT",VERTEX,{"disambiguationData":[OD(0.0)],"derivedFrom":[subQ1,subQ0]});Q84=makeQuery(id+"F25.imprint","IMPRINT",FACE,{"disambiguationData":[TD([[makeQuery(id+"F25.imprint","IMPRINT",EDGE,{"disambiguationData":[TD([[subQ2,-1.0]])],"derivedFrom":subQ0}),1.0]])]});}
            var Q85;
            {var subQ0=sQuery(id+"F25.wireOp",EDGE,"E65.20.0");var subQ1=makeQuery(id+"F24.opExtrude","CAP_EDGE",EDGE,{"disambiguationData":[OSD([sQuery(id+"F23.wireOp",EDGE,"E44")])],"isStart":false});var subQ2=makeQuery(id+"F25.imprint","INTERSECT",VERTEX,{"disambiguationData":[OD(0.0)],"derivedFrom":[subQ1,subQ0]});Q85=makeQuery(id+"F25.imprint","IMPRINT",FACE,{"disambiguationData":[TD([[makeQuery(id+"F25.imprint","IMPRINT",EDGE,{"disambiguationData":[TD([[subQ2,1.0]])],"derivedFrom":subQ0}),1.0]])]});}
            var Q86;
            {var subQ0=sQuery(id+"F25.wireOp",EDGE,"E65.19.0");var subQ1=makeQuery(id+"F24.opExtrude","CAP_EDGE",EDGE,{"disambiguationData":[OSD([sQuery(id+"F23.wireOp",EDGE,"E44")])],"isStart":false});var subQ2=makeQuery(id+"F25.imprint","INTERSECT",VERTEX,{"disambiguationData":[OD(0.0)],"derivedFrom":[subQ1,subQ0]});Q86=makeQuery(id+"F25.imprint","IMPRINT",FACE,{"disambiguationData":[TD([[makeQuery(id+"F25.imprint","IMPRINT",EDGE,{"disambiguationData":[TD([[subQ2,1.0]])],"derivedFrom":subQ0}),1.0]])]});}
            var Q87;
            {var subQ0=sQuery(id+"F25.wireOp",EDGE,"E65.19.0");var subQ1=makeQuery(id+"F24.opExtrude","CAP_EDGE",EDGE,{"disambiguationData":[OSD([sQuery(id+"F23.wireOp",EDGE,"E44")])],"isStart":false});var subQ2=makeQuery(id+"F25.imprint","INTERSECT",VERTEX,{"disambiguationData":[OD(0.0)],"derivedFrom":[subQ1,subQ0]});Q87=makeQuery(id+"F25.imprint","IMPRINT",FACE,{"disambiguationData":[TD([[makeQuery(id+"F25.imprint","IMPRINT",EDGE,{"disambiguationData":[TD([[subQ2,-1.0]])],"derivedFrom":subQ0}),1.0]])]});}
            var Q88;
            {var subQ0=sQuery(id+"F25.wireOp",EDGE,"E65.18.0");var subQ1=makeQuery(id+"F24.opExtrude","CAP_EDGE",EDGE,{"disambiguationData":[OSD([sQuery(id+"F23.wireOp",EDGE,"E44")])],"isStart":false});var subQ2=makeQuery(id+"F25.imprint","INTERSECT",VERTEX,{"disambiguationData":[OD(0.0)],"derivedFrom":[subQ1,subQ0]});Q88=makeQuery(id+"F25.imprint","IMPRINT",FACE,{"disambiguationData":[TD([[makeQuery(id+"F25.imprint","IMPRINT",EDGE,{"disambiguationData":[TD([[subQ2,-1.0]])],"derivedFrom":subQ0}),1.0]])]});}
            var Q89;
            {var subQ0=sQuery(id+"F25.wireOp",EDGE,"E65.18.0");var subQ1=makeQuery(id+"F24.opExtrude","CAP_EDGE",EDGE,{"disambiguationData":[OSD([sQuery(id+"F23.wireOp",EDGE,"E44")])],"isStart":false});var subQ2=makeQuery(id+"F25.imprint","INTERSECT",VERTEX,{"disambiguationData":[OD(0.0)],"derivedFrom":[subQ1,subQ0]});Q89=makeQuery(id+"F25.imprint","IMPRINT",FACE,{"disambiguationData":[TD([[makeQuery(id+"F25.imprint","IMPRINT",EDGE,{"disambiguationData":[TD([[subQ2,1.0]])],"derivedFrom":subQ0}),1.0]])]});}
            var Q90;
            {var subQ0=sQuery(id+"F25.wireOp",EDGE,"E65.17.0");var subQ1=makeQuery(id+"F24.opExtrude","CAP_EDGE",EDGE,{"disambiguationData":[OSD([sQuery(id+"F23.wireOp",EDGE,"E44")])],"isStart":false});var subQ2=makeQuery(id+"F25.imprint","INTERSECT",VERTEX,{"disambiguationData":[OD(0.0)],"derivedFrom":[subQ1,subQ0]});Q90=makeQuery(id+"F25.imprint","IMPRINT",FACE,{"disambiguationData":[TD([[makeQuery(id+"F25.imprint","IMPRINT",EDGE,{"disambiguationData":[TD([[subQ2,1.0]])],"derivedFrom":subQ0}),1.0]])]});}
            var Q91;
            {var subQ0=sQuery(id+"F25.wireOp",EDGE,"E65.17.0");var subQ1=makeQuery(id+"F24.opExtrude","CAP_EDGE",EDGE,{"disambiguationData":[OSD([sQuery(id+"F23.wireOp",EDGE,"E44")])],"isStart":false});var subQ2=makeQuery(id+"F25.imprint","INTERSECT",VERTEX,{"disambiguationData":[OD(0.0)],"derivedFrom":[subQ1,subQ0]});Q91=makeQuery(id+"F25.imprint","IMPRINT",FACE,{"disambiguationData":[TD([[makeQuery(id+"F25.imprint","IMPRINT",EDGE,{"disambiguationData":[TD([[subQ2,-1.0]])],"derivedFrom":subQ0}),1.0]])]});}
            var Q92;
            {var subQ0=sQuery(id+"F25.wireOp",EDGE,"E65.16.0");var subQ1=makeQuery(id+"F24.opExtrude","CAP_EDGE",EDGE,{"disambiguationData":[OSD([sQuery(id+"F23.wireOp",EDGE,"E44")])],"isStart":false});var subQ2=makeQuery(id+"F25.imprint","INTERSECT",VERTEX,{"disambiguationData":[OD(0.0)],"derivedFrom":[subQ1,subQ0]});Q92=makeQuery(id+"F25.imprint","IMPRINT",FACE,{"disambiguationData":[TD([[makeQuery(id+"F25.imprint","IMPRINT",EDGE,{"disambiguationData":[TD([[subQ2,-1.0]])],"derivedFrom":subQ0}),1.0]])]});}
            var Q93;
            {var subQ0=sQuery(id+"F25.wireOp",EDGE,"E65.16.0");var subQ1=makeQuery(id+"F24.opExtrude","CAP_EDGE",EDGE,{"disambiguationData":[OSD([sQuery(id+"F23.wireOp",EDGE,"E44")])],"isStart":false});var subQ2=makeQuery(id+"F25.imprint","INTERSECT",VERTEX,{"disambiguationData":[OD(0.0)],"derivedFrom":[subQ1,subQ0]});Q93=makeQuery(id+"F25.imprint","IMPRINT",FACE,{"disambiguationData":[TD([[makeQuery(id+"F25.imprint","IMPRINT",EDGE,{"disambiguationData":[TD([[subQ2,1.0]])],"derivedFrom":subQ0}),1.0]])]});}
            var Q94;
            {var subQ0=sQuery(id+"F25.wireOp",EDGE,"E65.15.0");var subQ1=makeQuery(id+"F24.opExtrude","CAP_EDGE",EDGE,{"disambiguationData":[OSD([sQuery(id+"F23.wireOp",EDGE,"E44")])],"isStart":false});var subQ2=makeQuery(id+"F25.imprint","INTERSECT",VERTEX,{"disambiguationData":[OD(0.0)],"derivedFrom":[subQ1,subQ0]});Q94=makeQuery(id+"F25.imprint","IMPRINT",FACE,{"disambiguationData":[TD([[makeQuery(id+"F25.imprint","IMPRINT",EDGE,{"disambiguationData":[TD([[subQ2,1.0]])],"derivedFrom":subQ0}),1.0]])]});}
            var Q95;
            {var subQ0=sQuery(id+"F25.wireOp",EDGE,"E65.15.0");var subQ1=makeQuery(id+"F24.opExtrude","CAP_EDGE",EDGE,{"disambiguationData":[OSD([sQuery(id+"F23.wireOp",EDGE,"E44")])],"isStart":false});var subQ2=makeQuery(id+"F25.imprint","INTERSECT",VERTEX,{"disambiguationData":[OD(0.0)],"derivedFrom":[subQ1,subQ0]});Q95=makeQuery(id+"F25.imprint","IMPRINT",FACE,{"disambiguationData":[TD([[makeQuery(id+"F25.imprint","IMPRINT",EDGE,{"disambiguationData":[TD([[subQ2,-1.0]])],"derivedFrom":subQ0}),1.0]])]});}
            var Q96;
            {var subQ0=sQuery(id+"F25.wireOp",EDGE,"E65.14.0");var subQ1=makeQuery(id+"F24.opExtrude","CAP_EDGE",EDGE,{"disambiguationData":[OSD([sQuery(id+"F23.wireOp",EDGE,"E44")])],"isStart":false});var subQ2=makeQuery(id+"F25.imprint","INTERSECT",VERTEX,{"disambiguationData":[OD(0.0)],"derivedFrom":[subQ1,subQ0]});Q96=makeQuery(id+"F25.imprint","IMPRINT",FACE,{"disambiguationData":[TD([[makeQuery(id+"F25.imprint","IMPRINT",EDGE,{"disambiguationData":[TD([[subQ2,1.0]])],"derivedFrom":subQ0}),1.0]])]});}
            var Q97;
            {var subQ0=sQuery(id+"F25.wireOp",EDGE,"E65.14.0");var subQ1=makeQuery(id+"F24.opExtrude","CAP_EDGE",EDGE,{"disambiguationData":[OSD([sQuery(id+"F23.wireOp",EDGE,"E44")])],"isStart":false});var subQ2=makeQuery(id+"F25.imprint","INTERSECT",VERTEX,{"disambiguationData":[OD(0.0)],"derivedFrom":[subQ1,subQ0]});Q97=makeQuery(id+"F25.imprint","IMPRINT",FACE,{"disambiguationData":[TD([[makeQuery(id+"F25.imprint","IMPRINT",EDGE,{"disambiguationData":[TD([[subQ2,-1.0]])],"derivedFrom":subQ0}),1.0]])]});}
            var Q98;
            {var subQ0=sQuery(id+"F25.wireOp",EDGE,"E65.13.0");var subQ1=makeQuery(id+"F24.opExtrude","CAP_EDGE",EDGE,{"disambiguationData":[OSD([sQuery(id+"F23.wireOp",EDGE,"E44")])],"isStart":false});var subQ2=makeQuery(id+"F25.imprint","INTERSECT",VERTEX,{"disambiguationData":[OD(0.0)],"derivedFrom":[subQ1,subQ0]});Q98=makeQuery(id+"F25.imprint","IMPRINT",FACE,{"disambiguationData":[TD([[makeQuery(id+"F25.imprint","IMPRINT",EDGE,{"disambiguationData":[TD([[subQ2,-1.0]])],"derivedFrom":subQ0}),1.0]])]});}
            var Q99;
            {var subQ0=sQuery(id+"F25.wireOp",EDGE,"E65.13.0");var subQ1=makeQuery(id+"F24.opExtrude","CAP_EDGE",EDGE,{"disambiguationData":[OSD([sQuery(id+"F23.wireOp",EDGE,"E44")])],"isStart":false});var subQ2=makeQuery(id+"F25.imprint","INTERSECT",VERTEX,{"disambiguationData":[OD(0.0)],"derivedFrom":[subQ1,subQ0]});Q99=makeQuery(id+"F25.imprint","IMPRINT",FACE,{"disambiguationData":[TD([[makeQuery(id+"F25.imprint","IMPRINT",EDGE,{"disambiguationData":[TD([[subQ2,1.0]])],"derivedFrom":subQ0}),1.0]])]});}
            var Q100;
            {var subQ0=sQuery(id+"F25.wireOp",EDGE,"E65.12.0");var subQ1=makeQuery(id+"F24.opExtrude","CAP_EDGE",EDGE,{"disambiguationData":[OSD([sQuery(id+"F23.wireOp",EDGE,"E44")])],"isStart":false});var subQ2=makeQuery(id+"F25.imprint","INTERSECT",VERTEX,{"disambiguationData":[OD(0.0)],"derivedFrom":[subQ1,subQ0]});Q100=makeQuery(id+"F25.imprint","IMPRINT",FACE,{"disambiguationData":[TD([[makeQuery(id+"F25.imprint","IMPRINT",EDGE,{"disambiguationData":[TD([[subQ2,1.0]])],"derivedFrom":subQ0}),1.0]])]});}
            var Q101;
            {var subQ0=sQuery(id+"F25.wireOp",EDGE,"E65.12.0");var subQ1=makeQuery(id+"F24.opExtrude","CAP_EDGE",EDGE,{"disambiguationData":[OSD([sQuery(id+"F23.wireOp",EDGE,"E44")])],"isStart":false});var subQ2=makeQuery(id+"F25.imprint","INTERSECT",VERTEX,{"disambiguationData":[OD(0.0)],"derivedFrom":[subQ1,subQ0]});Q101=makeQuery(id+"F25.imprint","IMPRINT",FACE,{"disambiguationData":[TD([[makeQuery(id+"F25.imprint","IMPRINT",EDGE,{"disambiguationData":[TD([[subQ2,-1.0]])],"derivedFrom":subQ0}),1.0]])]});}
            var Q102;
            {var subQ0=sQuery(id+"F25.wireOp",EDGE,"E65.11.0");var subQ1=makeQuery(id+"F24.opExtrude","CAP_EDGE",EDGE,{"disambiguationData":[OSD([sQuery(id+"F23.wireOp",EDGE,"E44")])],"isStart":false});var subQ2=makeQuery(id+"F25.imprint","INTERSECT",VERTEX,{"disambiguationData":[OD(0.0)],"derivedFrom":[subQ1,subQ0]});Q102=makeQuery(id+"F25.imprint","IMPRINT",FACE,{"disambiguationData":[TD([[makeQuery(id+"F25.imprint","IMPRINT",EDGE,{"disambiguationData":[TD([[subQ2,-1.0]])],"derivedFrom":subQ0}),1.0]])]});}
            var Q103;
            {var subQ0=sQuery(id+"F25.wireOp",EDGE,"E65.11.0");var subQ1=makeQuery(id+"F24.opExtrude","CAP_EDGE",EDGE,{"disambiguationData":[OSD([sQuery(id+"F23.wireOp",EDGE,"E44")])],"isStart":false});var subQ2=makeQuery(id+"F25.imprint","INTERSECT",VERTEX,{"disambiguationData":[OD(0.0)],"derivedFrom":[subQ1,subQ0]});Q103=makeQuery(id+"F25.imprint","IMPRINT",FACE,{"disambiguationData":[TD([[makeQuery(id+"F25.imprint","IMPRINT",EDGE,{"disambiguationData":[TD([[subQ2,1.0]])],"derivedFrom":subQ0}),1.0]])]});}
            var Q104;
            {var subQ0=sQuery(id+"F25.wireOp",EDGE,"E65.10.0");var subQ1=makeQuery(id+"F24.opExtrude","CAP_EDGE",EDGE,{"disambiguationData":[OSD([sQuery(id+"F23.wireOp",EDGE,"E44")])],"isStart":false});var subQ2=makeQuery(id+"F25.imprint","INTERSECT",VERTEX,{"disambiguationData":[OD(0.0)],"derivedFrom":[subQ1,subQ0]});Q104=makeQuery(id+"F25.imprint","IMPRINT",FACE,{"disambiguationData":[TD([[makeQuery(id+"F25.imprint","IMPRINT",EDGE,{"disambiguationData":[TD([[subQ2,1.0]])],"derivedFrom":subQ0}),1.0]])]});}
            var Q105;
            {var subQ0=sQuery(id+"F25.wireOp",EDGE,"E65.10.0");var subQ1=makeQuery(id+"F24.opExtrude","CAP_EDGE",EDGE,{"disambiguationData":[OSD([sQuery(id+"F23.wireOp",EDGE,"E44")])],"isStart":false});var subQ2=makeQuery(id+"F25.imprint","INTERSECT",VERTEX,{"disambiguationData":[OD(0.0)],"derivedFrom":[subQ1,subQ0]});Q105=makeQuery(id+"F25.imprint","IMPRINT",FACE,{"disambiguationData":[TD([[makeQuery(id+"F25.imprint","IMPRINT",EDGE,{"disambiguationData":[TD([[subQ2,-1.0]])],"derivedFrom":subQ0}),1.0]])]});}
            var Q106;
            {var subQ0=sQuery(id+"F25.wireOp",EDGE,"E65.9.0");var subQ1=makeQuery(id+"F24.opExtrude","CAP_EDGE",EDGE,{"disambiguationData":[OSD([sQuery(id+"F23.wireOp",EDGE,"E44")])],"isStart":false});var subQ2=makeQuery(id+"F25.imprint","INTERSECT",VERTEX,{"disambiguationData":[OD(0.0)],"derivedFrom":[subQ1,subQ0]});Q106=makeQuery(id+"F25.imprint","IMPRINT",FACE,{"disambiguationData":[TD([[makeQuery(id+"F25.imprint","IMPRINT",EDGE,{"disambiguationData":[TD([[subQ2,1.0]])],"derivedFrom":subQ0}),1.0]])]});}
            var Q107;
            {var subQ0=sQuery(id+"F25.wireOp",EDGE,"E65.9.0");var subQ1=makeQuery(id+"F24.opExtrude","CAP_EDGE",EDGE,{"disambiguationData":[OSD([sQuery(id+"F23.wireOp",EDGE,"E44")])],"isStart":false});var subQ2=makeQuery(id+"F25.imprint","INTERSECT",VERTEX,{"disambiguationData":[OD(0.0)],"derivedFrom":[subQ1,subQ0]});Q107=makeQuery(id+"F25.imprint","IMPRINT",FACE,{"disambiguationData":[TD([[makeQuery(id+"F25.imprint","IMPRINT",EDGE,{"disambiguationData":[TD([[subQ2,-1.0]])],"derivedFrom":subQ0}),1.0]])]});}
            var Q108;
            {var subQ0=sQuery(id+"F25.wireOp",EDGE,"E65.8.0");var subQ1=makeQuery(id+"F24.opExtrude","CAP_EDGE",EDGE,{"disambiguationData":[OSD([sQuery(id+"F23.wireOp",EDGE,"E44")])],"isStart":false});var subQ2=makeQuery(id+"F25.imprint","INTERSECT",VERTEX,{"disambiguationData":[OD(0.0)],"derivedFrom":[subQ1,subQ0]});Q108=makeQuery(id+"F25.imprint","IMPRINT",FACE,{"disambiguationData":[TD([[makeQuery(id+"F25.imprint","IMPRINT",EDGE,{"disambiguationData":[TD([[subQ2,1.0]])],"derivedFrom":subQ0}),1.0]])]});}
            var Q109;
            {var subQ0=sQuery(id+"F25.wireOp",EDGE,"E65.8.0");var subQ1=makeQuery(id+"F24.opExtrude","CAP_EDGE",EDGE,{"disambiguationData":[OSD([sQuery(id+"F23.wireOp",EDGE,"E44")])],"isStart":false});var subQ2=makeQuery(id+"F25.imprint","INTERSECT",VERTEX,{"disambiguationData":[OD(0.0)],"derivedFrom":[subQ1,subQ0]});Q109=makeQuery(id+"F25.imprint","IMPRINT",FACE,{"disambiguationData":[TD([[makeQuery(id+"F25.imprint","IMPRINT",EDGE,{"disambiguationData":[TD([[subQ2,-1.0]])],"derivedFrom":subQ0}),1.0]])]});}
            var Q110;
            {var subQ0=sQuery(id+"F25.wireOp",EDGE,"E65.7.0");var subQ1=makeQuery(id+"F24.opExtrude","CAP_EDGE",EDGE,{"disambiguationData":[OSD([sQuery(id+"F23.wireOp",EDGE,"E44")])],"isStart":false});var subQ2=makeQuery(id+"F25.imprint","INTERSECT",VERTEX,{"disambiguationData":[OD(0.0)],"derivedFrom":[subQ1,subQ0]});Q110=makeQuery(id+"F25.imprint","IMPRINT",FACE,{"disambiguationData":[TD([[makeQuery(id+"F25.imprint","IMPRINT",EDGE,{"disambiguationData":[TD([[subQ2,1.0]])],"derivedFrom":subQ0}),1.0]])]});}
            var Q111;
            {var subQ0=sQuery(id+"F25.wireOp",EDGE,"E65.7.0");var subQ1=makeQuery(id+"F24.opExtrude","CAP_EDGE",EDGE,{"disambiguationData":[OSD([sQuery(id+"F23.wireOp",EDGE,"E44")])],"isStart":false});var subQ2=makeQuery(id+"F25.imprint","INTERSECT",VERTEX,{"disambiguationData":[OD(0.0)],"derivedFrom":[subQ1,subQ0]});Q111=makeQuery(id+"F25.imprint","IMPRINT",FACE,{"disambiguationData":[TD([[makeQuery(id+"F25.imprint","IMPRINT",EDGE,{"disambiguationData":[TD([[subQ2,-1.0]])],"derivedFrom":subQ0}),1.0]])]});}
            var Q112;
            {var subQ0=sQuery(id+"F25.wireOp",EDGE,"E65.6.0");var subQ1=makeQuery(id+"F24.opExtrude","CAP_EDGE",EDGE,{"disambiguationData":[OSD([sQuery(id+"F23.wireOp",EDGE,"E44")])],"isStart":false});var subQ2=makeQuery(id+"F25.imprint","INTERSECT",VERTEX,{"disambiguationData":[OD(0.0)],"derivedFrom":[subQ1,subQ0]});Q112=makeQuery(id+"F25.imprint","IMPRINT",FACE,{"disambiguationData":[TD([[makeQuery(id+"F25.imprint","IMPRINT",EDGE,{"disambiguationData":[TD([[subQ2,1.0]])],"derivedFrom":subQ0}),1.0]])]});}
            var Q113;
            {var subQ0=sQuery(id+"F25.wireOp",EDGE,"E65.6.0");var subQ1=makeQuery(id+"F24.opExtrude","CAP_EDGE",EDGE,{"disambiguationData":[OSD([sQuery(id+"F23.wireOp",EDGE,"E44")])],"isStart":false});var subQ2=makeQuery(id+"F25.imprint","INTERSECT",VERTEX,{"disambiguationData":[OD(0.0)],"derivedFrom":[subQ1,subQ0]});Q113=makeQuery(id+"F25.imprint","IMPRINT",FACE,{"disambiguationData":[TD([[makeQuery(id+"F25.imprint","IMPRINT",EDGE,{"disambiguationData":[TD([[subQ2,-1.0]])],"derivedFrom":subQ0}),1.0]])]});}
            var Q114;
            {var subQ0=sQuery(id+"F25.wireOp",EDGE,"E65.5.0");var subQ1=makeQuery(id+"F24.opExtrude","CAP_EDGE",EDGE,{"disambiguationData":[OSD([sQuery(id+"F23.wireOp",EDGE,"E44")])],"isStart":false});var subQ2=makeQuery(id+"F25.imprint","INTERSECT",VERTEX,{"disambiguationData":[OD(0.0)],"derivedFrom":[subQ1,subQ0]});Q114=makeQuery(id+"F25.imprint","IMPRINT",FACE,{"disambiguationData":[TD([[makeQuery(id+"F25.imprint","IMPRINT",EDGE,{"disambiguationData":[TD([[subQ2,1.0]])],"derivedFrom":subQ0}),1.0]])]});}
            var Q115;
            {var subQ0=sQuery(id+"F25.wireOp",EDGE,"E65.5.0");var subQ1=makeQuery(id+"F24.opExtrude","CAP_EDGE",EDGE,{"disambiguationData":[OSD([sQuery(id+"F23.wireOp",EDGE,"E44")])],"isStart":false});var subQ2=makeQuery(id+"F25.imprint","INTERSECT",VERTEX,{"disambiguationData":[OD(0.0)],"derivedFrom":[subQ1,subQ0]});Q115=makeQuery(id+"F25.imprint","IMPRINT",FACE,{"disambiguationData":[TD([[makeQuery(id+"F25.imprint","IMPRINT",EDGE,{"disambiguationData":[TD([[subQ2,-1.0]])],"derivedFrom":subQ0}),1.0]])]});}
            var Q116;
            {var subQ0=sQuery(id+"F25.wireOp",EDGE,"E65.4.0");var subQ1=makeQuery(id+"F24.opExtrude","CAP_EDGE",EDGE,{"disambiguationData":[OSD([sQuery(id+"F23.wireOp",EDGE,"E44")])],"isStart":false});var subQ2=makeQuery(id+"F25.imprint","INTERSECT",VERTEX,{"disambiguationData":[OD(0.0)],"derivedFrom":[subQ1,subQ0]});Q116=makeQuery(id+"F25.imprint","IMPRINT",FACE,{"disambiguationData":[TD([[makeQuery(id+"F25.imprint","IMPRINT",EDGE,{"disambiguationData":[TD([[subQ2,1.0]])],"derivedFrom":subQ0}),1.0]])]});}
            var Q117;
            {var subQ0=sQuery(id+"F25.wireOp",EDGE,"E65.4.0");var subQ1=makeQuery(id+"F24.opExtrude","CAP_EDGE",EDGE,{"disambiguationData":[OSD([sQuery(id+"F23.wireOp",EDGE,"E44")])],"isStart":false});var subQ2=makeQuery(id+"F25.imprint","INTERSECT",VERTEX,{"disambiguationData":[OD(0.0)],"derivedFrom":[subQ1,subQ0]});Q117=makeQuery(id+"F25.imprint","IMPRINT",FACE,{"disambiguationData":[TD([[makeQuery(id+"F25.imprint","IMPRINT",EDGE,{"disambiguationData":[TD([[subQ2,-1.0]])],"derivedFrom":subQ0}),1.0]])]});}
            extrude(context, id + "F28", {"entities" : qUnion([Q0, Q1, Q2, Q3, Q4, Q5, Q6, Q7, Q8, Q9, Q10, Q11, Q12, Q13, Q14, Q15, Q16, Q17, Q18, Q19, Q20, Q21, Q22, Q23, Q24, Q25, Q26, Q27, Q28, Q29, Q30, Q31, Q32, Q33, Q34, Q35, Q36, Q37, Q38, Q39, Q40, Q41, Q42, Q43, Q44, Q45, Q46, Q47, Q48, Q49, Q50, Q51, Q52, Q53, Q54, Q55, Q56, Q57, Q58, Q59, Q60, Q61, Q62, Q63, Q64, Q65, Q66, Q67, Q68, Q69, Q70, Q71, Q72, Q73, Q74, Q75, Q76, Q77, Q78, Q79, Q80, Q81, Q82, Q83, Q84, Q85, Q86, Q87, Q88, Q89, Q90, Q91, Q92, Q93, Q94, Q95, Q96, Q97, Q98, Q99, Q100, Q101, Q102, Q103, Q104, Q105, Q106, Q107, Q108, Q109, Q110, Q111, Q112, Q113, Q114, Q115, Q116, Q117]), "operationType" : NewBodyOperationType.ADD, "depth" : 4.7 * mm, "offsetDistance" : 25 * mm, "hasSecondDirection" : true, "secondDirectionOppositeDirection" : false, "secondDirectionDepth" : 0.1 * mm});
        }
        {
            var Q0;
            Q0=makeQuery(id+"F27.boolean.opBoolean","MERGE",FACE,{"derivedFrom":[makeQuery(id+"F26.opExtrude","CAP_FACE",FACE,{"disambiguationData":[OSD([sQuery(id+"F25.wireOp",EDGE,"E58"),sQuery(id+"F25.wireOp",EDGE,"E59")])],"isStart":false}),makeQuery(id+"F27.opExtrude","CAP_FACE",FACE,{"disambiguationData":[OSD([sQuery(id+"F6.wireOp",EDGE,"E20"),sQuery(id+"F23.wireOp",EDGE,"E43")])],"isStart":false})]});
            var sketch = newSketch(context, id + "F29", { "sketchPlane" : qUnion([Q0])});
            skCircle(sketch, "E72", {"center": v(0, 0) * mm, "radius": 55 * mm});
            skCircle(sketch, "E73", {"center": v(0, 0) * mm, "radius": 47.5 * mm});
            skCircle(sketch, "E74", {"center": v(0, 0) * mm, "radius": 46.25 * mm});
            skCircle(sketch, "E75", {"center": v(0, 0) * mm, "radius": 44 * mm});
            skSolve(sketch);
        }
        {
            var Q0;
            Q0=makeQuery(id+"F29.imprint","IMPRINT",FACE,{"disambiguationData":[TD([[makeQuery(id+"F29.imprint","IMPRINT",EDGE,{"derivedFrom":sQuery(id+"F29.wireOp",EDGE,"E72")}),1.0]])]});
            var Q1;
            Q1=makeQuery(id+"F29.imprint","IMPRINT",FACE,{"disambiguationData":[TD([[makeQuery(id+"F29.imprint","IMPRINT",EDGE,{"derivedFrom":sQuery(id+"F29.wireOp",EDGE,"E73")}),-1.0]])]});
            extrude(context, id + "F30", {"entities" : qUnion([Q0, Q1]), "depth" : 1 * mm, "offsetDistance" : 25 * mm});
        }
        {
            var Q0;
            Q0=makeQuery(id+"F29.imprint","IMPRINT",FACE,{"disambiguationData":[TD([[makeQuery(id+"F29.imprint","IMPRINT",EDGE,{"derivedFrom":sQuery(id+"F29.wireOp",EDGE,"E74")}),1.0]])]});
            extrude(context, id + "F31", {"entities" : qUnion([Q0]), "depth" : 0.8 * mm, "offsetDistance" : 25 * mm});
        }
    });
